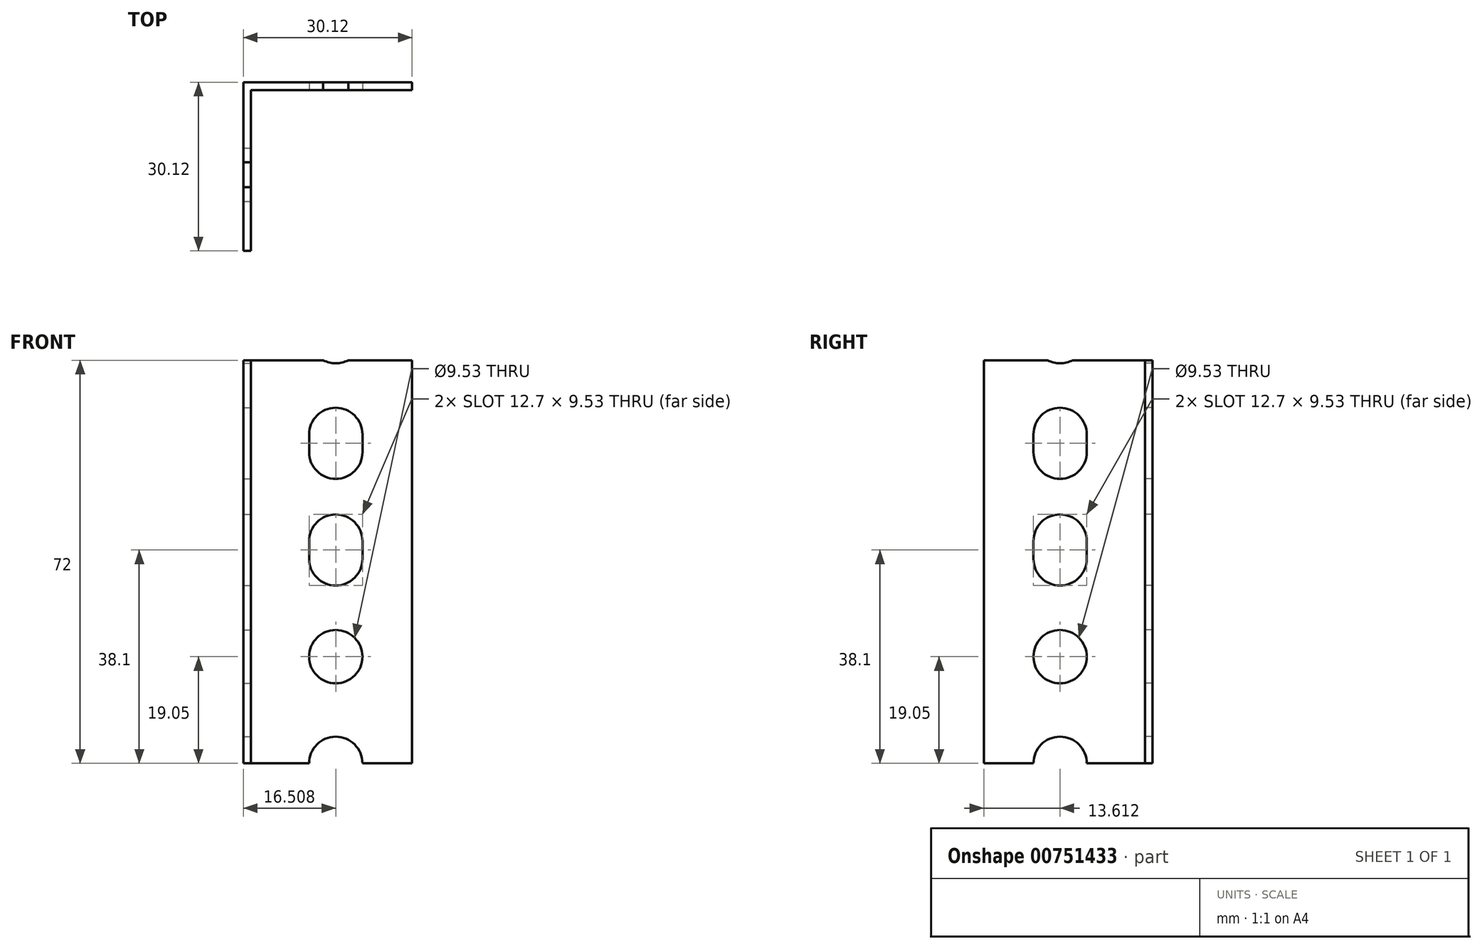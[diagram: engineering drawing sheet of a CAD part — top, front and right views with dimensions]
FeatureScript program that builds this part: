
annotation { "Feature Type Name" : "Feature", "Feature Type Description" : "" }
export const myFeature = defineFeature(function(context is Context, id is Id, definition is map)
    precondition{}
    {
        {
            assignVariable(context, id + "F0", {"name" : "height", "anyValue" : 72});
        }
        {
            var Q0;
            Q0=qCreatedBy(makeId("Top.planeOp"),FACE);
            var sketch = newSketch(context, id + "F1", { "sketchPlane" : qUnion([Q0])});
            skLineSegment(sketch, "E0", {"start": v(-1.37, -28.75) * mm, "end": v(-1.37, 1.37) * mm});
            skLineSegment(sketch, "E1", {"start": v(-1.37, 1.37) * mm, "end": v(28.75, 1.37) * mm});
            skLineSegment(sketch, "E2", {"start": v(28.75, 1.37) * mm, "end": v(28.75, 0) * mm});
            skLineSegment(sketch, "E3", {"start": v(28.75, 0) * mm, "end": v(0, 0) * mm});
            skLineSegment(sketch, "E4", {"start": v(0, 0) * mm, "end": v(0, -28.75) * mm});
            skLineSegment(sketch, "E5", {"start": v(0, -28.75) * mm, "end": v(-1.37, -28.75) * mm});
            skSolve(sketch);
        }
        {
            var Q0;
            Q0=makeQuery(id+"F1.imprint","IMPRINT",FACE,{"disambiguationData":[TD([[makeQuery(id+"F1.imprint","IMPRINT",EDGE,{"derivedFrom":sQuery(id+"F1.wireOp",EDGE,"E0")}),-1.0]])]});
            extrude(context, id + "F2", {"entities" : qUnion([Q0]), "depth" : (getVariable(context, 'height')) * mm, "offsetDistance" : 25.4 * mm});
        }
        {
            var Q0;
            Q0=makeQuery(id+"F2.opExtrude","SWEPT_FACE",FACE,{"disambiguationData":[OSD([sQuery(id+"F1.wireOp",EDGE,"E3")])]});
            var sketch = newSketch(context, id + "F3", { "sketchPlane" : qUnion([Q0])});
            skPoint(sketch, "E6", {"position": v(15.14, 19.05) * mm});
            skLineSegment(sketch, "E7", {"start": v(15.14, 0) * mm, "end": v(15.14, 1828.8) * mm, "construction": true});
            skCircle(sketch, "E8", {"center": v(15.14, 19.05) * mm, "radius": 4.76 * mm});
            skCircle(sketch, "E9", {"center": v(15.14, 0) * mm, "radius": 4.76 * mm});
            skPoint(sketch, "E10", {"position": v(15.14, 38.1) * mm});
            skPoint(sketch, "E11", {"position": v(15.14, 57.15) * mm});
            skArc(sketch, "E12", {"start": v(19.9, 39.69) * mm, "mid": v(15.14, 44.45) * mm, "end": v(10.38, 39.69) * mm});
            skArc(sketch, "E13", {"start": v(10.38, 36.51) * mm, "mid": v(15.14, 31.75) * mm, "end": v(19.9, 36.51) * mm});
            skLineSegment(sketch, "E14", {"start": v(19.9, 39.69) * mm, "end": v(19.9, 36.51) * mm});
            skLineSegment(sketch, "E15", {"start": v(10.38, 39.69) * mm, "end": v(10.38, 36.51) * mm});
            skArc(sketch, "E16", {"start": v(19.9, 58.74) * mm, "mid": v(15.14, 63.5) * mm, "end": v(10.38, 58.74) * mm});
            skArc(sketch, "E17", {"start": v(10.38, 55.56) * mm, "mid": v(15.14, 50.8) * mm, "end": v(19.9, 55.56) * mm});
            skLineSegment(sketch, "E18", {"start": v(19.9, 58.74) * mm, "end": v(19.9, 55.56) * mm});
            skLineSegment(sketch, "E19", {"start": v(10.38, 58.74) * mm, "end": v(10.38, 55.56) * mm});
            skPoint(sketch, "E20.0.1.0", {"position": v(15.14, 133.35) * mm});
            skArc(sketch, "E20.0.1.1", {"start": v(19.9, 134.94) * mm, "mid": v(15.14, 139.7) * mm, "end": v(10.38, 134.94) * mm});
            skPoint(sketch, "E20.0.1.2", {"position": v(15.14, 114.3) * mm});
            skPoint(sketch, "E20.0.1.3", {"position": v(15.14, 95.25) * mm});
            skArc(sketch, "E20.0.1.4", {"start": v(10.38, 131.76) * mm, "mid": v(15.14, 127) * mm, "end": v(19.9, 131.76) * mm});
            skCircle(sketch, "E20.0.1.5", {"center": v(15.14, 95.25) * mm, "radius": 4.76 * mm});
            skCircle(sketch, "E20.0.1.6", {"center": v(15.14, 76.2) * mm, "radius": 4.76 * mm});
            skArc(sketch, "E20.0.1.7", {"start": v(19.9, 115.89) * mm, "mid": v(15.14, 120.65) * mm, "end": v(10.38, 115.89) * mm});
            skArc(sketch, "E20.0.1.8", {"start": v(10.38, 112.71) * mm, "mid": v(15.14, 107.95) * mm, "end": v(19.9, 112.71) * mm});
            skPoint(sketch, "E20.0.1.9", {"position": v(15.14, 133.35) * mm});
            skPoint(sketch, "E20.0.1.10", {"position": v(15.14, 114.3) * mm});
            skLineSegment(sketch, "E20.0.1.11", {"start": v(10.38, 134.94) * mm, "end": v(10.38, 131.76) * mm});
            skLineSegment(sketch, "E20.0.1.12", {"start": v(19.9, 134.94) * mm, "end": v(19.9, 131.76) * mm});
            skLineSegment(sketch, "E20.0.1.13", {"start": v(19.9, 115.89) * mm, "end": v(19.9, 112.71) * mm});
            skLineSegment(sketch, "E20.0.1.14", {"start": v(10.38, 115.89) * mm, "end": v(10.38, 112.71) * mm});
            skPoint(sketch, "E20.0.2.0", {"position": v(15.14, 209.55) * mm});
            skArc(sketch, "E20.0.2.1", {"start": v(19.9, 211.14) * mm, "mid": v(15.14, 215.9) * mm, "end": v(10.38, 211.14) * mm});
            skPoint(sketch, "E20.0.2.2", {"position": v(15.14, 190.5) * mm});
            skPoint(sketch, "E20.0.2.3", {"position": v(15.14, 171.45) * mm});
            skArc(sketch, "E20.0.2.4", {"start": v(10.38, 207.96) * mm, "mid": v(15.14, 203.2) * mm, "end": v(19.9, 207.96) * mm});
            skCircle(sketch, "E20.0.2.5", {"center": v(15.14, 171.45) * mm, "radius": 4.76 * mm});
            skCircle(sketch, "E20.0.2.6", {"center": v(15.14, 152.4) * mm, "radius": 4.76 * mm});
            skArc(sketch, "E20.0.2.7", {"start": v(19.9, 192.09) * mm, "mid": v(15.14, 196.85) * mm, "end": v(10.38, 192.09) * mm});
            skArc(sketch, "E20.0.2.8", {"start": v(10.38, 188.91) * mm, "mid": v(15.14, 184.15) * mm, "end": v(19.9, 188.91) * mm});
            skPoint(sketch, "E20.0.2.9", {"position": v(15.14, 209.55) * mm});
            skPoint(sketch, "E20.0.2.10", {"position": v(15.14, 190.5) * mm});
            skLineSegment(sketch, "E20.0.2.11", {"start": v(10.38, 211.14) * mm, "end": v(10.38, 207.96) * mm});
            skLineSegment(sketch, "E20.0.2.12", {"start": v(19.9, 211.14) * mm, "end": v(19.9, 207.96) * mm});
            skLineSegment(sketch, "E20.0.2.13", {"start": v(19.9, 192.09) * mm, "end": v(19.9, 188.91) * mm});
            skLineSegment(sketch, "E20.0.2.14", {"start": v(10.38, 192.09) * mm, "end": v(10.38, 188.91) * mm});
            skPoint(sketch, "E20.0.3.0", {"position": v(15.14, 285.75) * mm});
            skArc(sketch, "E20.0.3.1", {"start": v(19.9, 287.34) * mm, "mid": v(15.14, 292.1) * mm, "end": v(10.38, 287.34) * mm});
            skPoint(sketch, "E20.0.3.2", {"position": v(15.14, 266.7) * mm});
            skPoint(sketch, "E20.0.3.3", {"position": v(15.14, 247.65) * mm});
            skArc(sketch, "E20.0.3.4", {"start": v(10.38, 284.16) * mm, "mid": v(15.14, 279.4) * mm, "end": v(19.9, 284.16) * mm});
            skCircle(sketch, "E20.0.3.5", {"center": v(15.14, 247.65) * mm, "radius": 4.76 * mm});
            skCircle(sketch, "E20.0.3.6", {"center": v(15.14, 228.6) * mm, "radius": 4.76 * mm});
            skArc(sketch, "E20.0.3.7", {"start": v(19.9, 268.29) * mm, "mid": v(15.14, 273.05) * mm, "end": v(10.38, 268.29) * mm});
            skArc(sketch, "E20.0.3.8", {"start": v(10.38, 265.11) * mm, "mid": v(15.14, 260.35) * mm, "end": v(19.9, 265.11) * mm});
            skPoint(sketch, "E20.0.3.9", {"position": v(15.14, 285.75) * mm});
            skPoint(sketch, "E20.0.3.10", {"position": v(15.14, 266.7) * mm});
            skLineSegment(sketch, "E20.0.3.11", {"start": v(10.38, 287.34) * mm, "end": v(10.38, 284.16) * mm});
            skLineSegment(sketch, "E20.0.3.12", {"start": v(19.9, 287.34) * mm, "end": v(19.9, 284.16) * mm});
            skLineSegment(sketch, "E20.0.3.13", {"start": v(19.9, 268.29) * mm, "end": v(19.9, 265.11) * mm});
            skLineSegment(sketch, "E20.0.3.14", {"start": v(10.38, 268.29) * mm, "end": v(10.38, 265.11) * mm});
            skPoint(sketch, "E20.0.4.0", {"position": v(15.14, 361.95) * mm});
            skArc(sketch, "E20.0.4.1", {"start": v(19.9, 363.54) * mm, "mid": v(15.14, 368.3) * mm, "end": v(10.38, 363.54) * mm});
            skPoint(sketch, "E20.0.4.2", {"position": v(15.14, 342.9) * mm});
            skPoint(sketch, "E20.0.4.3", {"position": v(15.14, 323.85) * mm});
            skArc(sketch, "E20.0.4.4", {"start": v(10.38, 360.36) * mm, "mid": v(15.14, 355.6) * mm, "end": v(19.9, 360.36) * mm});
            skCircle(sketch, "E20.0.4.5", {"center": v(15.14, 323.85) * mm, "radius": 4.76 * mm});
            skCircle(sketch, "E20.0.4.6", {"center": v(15.14, 304.8) * mm, "radius": 4.76 * mm});
            skArc(sketch, "E20.0.4.7", {"start": v(19.9, 344.49) * mm, "mid": v(15.14, 349.25) * mm, "end": v(10.38, 344.49) * mm});
            skArc(sketch, "E20.0.4.8", {"start": v(10.38, 341.31) * mm, "mid": v(15.14, 336.55) * mm, "end": v(19.9, 341.31) * mm});
            skPoint(sketch, "E20.0.4.9", {"position": v(15.14, 361.95) * mm});
            skPoint(sketch, "E20.0.4.10", {"position": v(15.14, 342.9) * mm});
            skLineSegment(sketch, "E20.0.4.11", {"start": v(10.38, 363.54) * mm, "end": v(10.38, 360.36) * mm});
            skLineSegment(sketch, "E20.0.4.12", {"start": v(19.9, 363.54) * mm, "end": v(19.9, 360.36) * mm});
            skLineSegment(sketch, "E20.0.4.13", {"start": v(19.9, 344.49) * mm, "end": v(19.9, 341.31) * mm});
            skLineSegment(sketch, "E20.0.4.14", {"start": v(10.38, 344.49) * mm, "end": v(10.38, 341.31) * mm});
            skPoint(sketch, "E20.0.5.0", {"position": v(15.14, 438.15) * mm});
            skArc(sketch, "E20.0.5.1", {"start": v(19.9, 439.74) * mm, "mid": v(15.14, 444.5) * mm, "end": v(10.38, 439.74) * mm});
            skPoint(sketch, "E20.0.5.2", {"position": v(15.14, 419.1) * mm});
            skPoint(sketch, "E20.0.5.3", {"position": v(15.14, 400.05) * mm});
            skArc(sketch, "E20.0.5.4", {"start": v(10.38, 436.56) * mm, "mid": v(15.14, 431.8) * mm, "end": v(19.9, 436.56) * mm});
            skCircle(sketch, "E20.0.5.5", {"center": v(15.14, 400.05) * mm, "radius": 4.76 * mm});
            skCircle(sketch, "E20.0.5.6", {"center": v(15.14, 381) * mm, "radius": 4.76 * mm});
            skArc(sketch, "E20.0.5.7", {"start": v(19.9, 420.69) * mm, "mid": v(15.14, 425.45) * mm, "end": v(10.38, 420.69) * mm});
            skArc(sketch, "E20.0.5.8", {"start": v(10.38, 417.51) * mm, "mid": v(15.14, 412.75) * mm, "end": v(19.9, 417.51) * mm});
            skPoint(sketch, "E20.0.5.9", {"position": v(15.14, 438.15) * mm});
            skPoint(sketch, "E20.0.5.10", {"position": v(15.14, 419.1) * mm});
            skLineSegment(sketch, "E20.0.5.11", {"start": v(10.38, 439.74) * mm, "end": v(10.38, 436.56) * mm});
            skLineSegment(sketch, "E20.0.5.12", {"start": v(19.9, 439.74) * mm, "end": v(19.9, 436.56) * mm});
            skLineSegment(sketch, "E20.0.5.13", {"start": v(19.9, 420.69) * mm, "end": v(19.9, 417.51) * mm});
            skLineSegment(sketch, "E20.0.5.14", {"start": v(10.38, 420.69) * mm, "end": v(10.38, 417.51) * mm});
            skPoint(sketch, "E20.0.6.0", {"position": v(15.14, 514.35) * mm});
            skArc(sketch, "E20.0.6.1", {"start": v(19.9, 515.94) * mm, "mid": v(15.14, 520.7) * mm, "end": v(10.38, 515.94) * mm});
            skPoint(sketch, "E20.0.6.2", {"position": v(15.14, 495.3) * mm});
            skPoint(sketch, "E20.0.6.3", {"position": v(15.14, 476.25) * mm});
            skArc(sketch, "E20.0.6.4", {"start": v(10.38, 512.76) * mm, "mid": v(15.14, 508) * mm, "end": v(19.9, 512.76) * mm});
            skCircle(sketch, "E20.0.6.5", {"center": v(15.14, 476.25) * mm, "radius": 4.76 * mm});
            skCircle(sketch, "E20.0.6.6", {"center": v(15.14, 457.2) * mm, "radius": 4.76 * mm});
            skArc(sketch, "E20.0.6.7", {"start": v(19.9, 496.89) * mm, "mid": v(15.14, 501.65) * mm, "end": v(10.38, 496.89) * mm});
            skArc(sketch, "E20.0.6.8", {"start": v(10.38, 493.71) * mm, "mid": v(15.14, 488.95) * mm, "end": v(19.9, 493.71) * mm});
            skPoint(sketch, "E20.0.6.9", {"position": v(15.14, 514.35) * mm});
            skPoint(sketch, "E20.0.6.10", {"position": v(15.14, 495.3) * mm});
            skLineSegment(sketch, "E20.0.6.11", {"start": v(10.38, 515.94) * mm, "end": v(10.38, 512.76) * mm});
            skLineSegment(sketch, "E20.0.6.12", {"start": v(19.9, 515.94) * mm, "end": v(19.9, 512.76) * mm});
            skLineSegment(sketch, "E20.0.6.13", {"start": v(19.9, 496.89) * mm, "end": v(19.9, 493.71) * mm});
            skLineSegment(sketch, "E20.0.6.14", {"start": v(10.38, 496.89) * mm, "end": v(10.38, 493.71) * mm});
            skPoint(sketch, "E20.0.7.0", {"position": v(15.14, 590.55) * mm});
            skArc(sketch, "E20.0.7.1", {"start": v(19.9, 592.14) * mm, "mid": v(15.14, 596.9) * mm, "end": v(10.38, 592.14) * mm});
            skPoint(sketch, "E20.0.7.2", {"position": v(15.14, 571.5) * mm});
            skPoint(sketch, "E20.0.7.3", {"position": v(15.14, 552.45) * mm});
            skArc(sketch, "E20.0.7.4", {"start": v(10.38, 588.96) * mm, "mid": v(15.14, 584.2) * mm, "end": v(19.9, 588.96) * mm});
            skCircle(sketch, "E20.0.7.5", {"center": v(15.14, 552.45) * mm, "radius": 4.76 * mm});
            skCircle(sketch, "E20.0.7.6", {"center": v(15.14, 533.4) * mm, "radius": 4.76 * mm});
            skArc(sketch, "E20.0.7.7", {"start": v(19.9, 573.09) * mm, "mid": v(15.14, 577.85) * mm, "end": v(10.38, 573.09) * mm});
            skArc(sketch, "E20.0.7.8", {"start": v(10.38, 569.91) * mm, "mid": v(15.14, 565.15) * mm, "end": v(19.9, 569.91) * mm});
            skPoint(sketch, "E20.0.7.9", {"position": v(15.14, 590.55) * mm});
            skPoint(sketch, "E20.0.7.10", {"position": v(15.14, 571.5) * mm});
            skLineSegment(sketch, "E20.0.7.11", {"start": v(10.38, 592.14) * mm, "end": v(10.38, 588.96) * mm});
            skLineSegment(sketch, "E20.0.7.12", {"start": v(19.9, 592.14) * mm, "end": v(19.9, 588.96) * mm});
            skLineSegment(sketch, "E20.0.7.13", {"start": v(19.9, 573.09) * mm, "end": v(19.9, 569.91) * mm});
            skLineSegment(sketch, "E20.0.7.14", {"start": v(10.38, 573.09) * mm, "end": v(10.38, 569.91) * mm});
            skPoint(sketch, "E20.0.8.0", {"position": v(15.14, 666.75) * mm});
            skArc(sketch, "E20.0.8.1", {"start": v(19.9, 668.34) * mm, "mid": v(15.14, 673.1) * mm, "end": v(10.38, 668.34) * mm});
            skPoint(sketch, "E20.0.8.2", {"position": v(15.14, 647.7) * mm});
            skPoint(sketch, "E20.0.8.3", {"position": v(15.14, 628.65) * mm});
            skArc(sketch, "E20.0.8.4", {"start": v(10.38, 665.16) * mm, "mid": v(15.14, 660.4) * mm, "end": v(19.9, 665.16) * mm});
            skCircle(sketch, "E20.0.8.5", {"center": v(15.14, 628.65) * mm, "radius": 4.76 * mm});
            skCircle(sketch, "E20.0.8.6", {"center": v(15.14, 609.6) * mm, "radius": 4.76 * mm});
            skArc(sketch, "E20.0.8.7", {"start": v(19.9, 649.29) * mm, "mid": v(15.14, 654.05) * mm, "end": v(10.38, 649.29) * mm});
            skArc(sketch, "E20.0.8.8", {"start": v(10.38, 646.11) * mm, "mid": v(15.14, 641.35) * mm, "end": v(19.9, 646.11) * mm});
            skPoint(sketch, "E20.0.8.9", {"position": v(15.14, 666.75) * mm});
            skPoint(sketch, "E20.0.8.10", {"position": v(15.14, 647.7) * mm});
            skLineSegment(sketch, "E20.0.8.11", {"start": v(10.38, 668.34) * mm, "end": v(10.38, 665.16) * mm});
            skLineSegment(sketch, "E20.0.8.12", {"start": v(19.9, 668.34) * mm, "end": v(19.9, 665.16) * mm});
            skLineSegment(sketch, "E20.0.8.13", {"start": v(19.9, 649.29) * mm, "end": v(19.9, 646.11) * mm});
            skLineSegment(sketch, "E20.0.8.14", {"start": v(10.38, 649.29) * mm, "end": v(10.38, 646.11) * mm});
            skPoint(sketch, "E20.0.9.0", {"position": v(15.14, 742.95) * mm});
            skArc(sketch, "E20.0.9.1", {"start": v(19.9, 744.54) * mm, "mid": v(15.14, 749.3) * mm, "end": v(10.38, 744.54) * mm});
            skPoint(sketch, "E20.0.9.2", {"position": v(15.14, 723.9) * mm});
            skPoint(sketch, "E20.0.9.3", {"position": v(15.14, 704.85) * mm});
            skArc(sketch, "E20.0.9.4", {"start": v(10.38, 741.36) * mm, "mid": v(15.14, 736.6) * mm, "end": v(19.9, 741.36) * mm});
            skCircle(sketch, "E20.0.9.5", {"center": v(15.14, 704.85) * mm, "radius": 4.76 * mm});
            skCircle(sketch, "E20.0.9.6", {"center": v(15.14, 685.8) * mm, "radius": 4.76 * mm});
            skArc(sketch, "E20.0.9.7", {"start": v(19.9, 725.49) * mm, "mid": v(15.14, 730.25) * mm, "end": v(10.38, 725.49) * mm});
            skArc(sketch, "E20.0.9.8", {"start": v(10.38, 722.31) * mm, "mid": v(15.14, 717.55) * mm, "end": v(19.9, 722.31) * mm});
            skPoint(sketch, "E20.0.9.9", {"position": v(15.14, 742.95) * mm});
            skPoint(sketch, "E20.0.9.10", {"position": v(15.14, 723.9) * mm});
            skLineSegment(sketch, "E20.0.9.11", {"start": v(10.38, 744.54) * mm, "end": v(10.38, 741.36) * mm});
            skLineSegment(sketch, "E20.0.9.12", {"start": v(19.9, 744.54) * mm, "end": v(19.9, 741.36) * mm});
            skLineSegment(sketch, "E20.0.9.13", {"start": v(19.9, 725.49) * mm, "end": v(19.9, 722.31) * mm});
            skLineSegment(sketch, "E20.0.9.14", {"start": v(10.38, 725.49) * mm, "end": v(10.38, 722.31) * mm});
            skPoint(sketch, "E20.0.10.0", {"position": v(15.14, 819.15) * mm});
            skArc(sketch, "E20.0.10.1", {"start": v(19.9, 820.74) * mm, "mid": v(15.14, 825.5) * mm, "end": v(10.38, 820.74) * mm});
            skPoint(sketch, "E20.0.10.2", {"position": v(15.14, 800.1) * mm});
            skPoint(sketch, "E20.0.10.3", {"position": v(15.14, 781.05) * mm});
            skArc(sketch, "E20.0.10.4", {"start": v(10.38, 817.56) * mm, "mid": v(15.14, 812.8) * mm, "end": v(19.9, 817.56) * mm});
            skCircle(sketch, "E20.0.10.5", {"center": v(15.14, 781.05) * mm, "radius": 4.76 * mm});
            skCircle(sketch, "E20.0.10.6", {"center": v(15.14, 762) * mm, "radius": 4.76 * mm});
            skArc(sketch, "E20.0.10.7", {"start": v(19.9, 801.69) * mm, "mid": v(15.14, 806.45) * mm, "end": v(10.38, 801.69) * mm});
            skArc(sketch, "E20.0.10.8", {"start": v(10.38, 798.51) * mm, "mid": v(15.14, 793.75) * mm, "end": v(19.9, 798.51) * mm});
            skPoint(sketch, "E20.0.10.9", {"position": v(15.14, 819.15) * mm});
            skPoint(sketch, "E20.0.10.10", {"position": v(15.14, 800.1) * mm});
            skLineSegment(sketch, "E20.0.10.11", {"start": v(10.38, 820.74) * mm, "end": v(10.38, 817.56) * mm});
            skLineSegment(sketch, "E20.0.10.12", {"start": v(19.9, 820.74) * mm, "end": v(19.9, 817.56) * mm});
            skLineSegment(sketch, "E20.0.10.13", {"start": v(19.9, 801.69) * mm, "end": v(19.9, 798.51) * mm});
            skLineSegment(sketch, "E20.0.10.14", {"start": v(10.38, 801.69) * mm, "end": v(10.38, 798.51) * mm});
            skPoint(sketch, "E20.0.11.0", {"position": v(15.14, 895.35) * mm});
            skArc(sketch, "E20.0.11.1", {"start": v(19.9, 896.94) * mm, "mid": v(15.14, 901.7) * mm, "end": v(10.38, 896.94) * mm});
            skPoint(sketch, "E20.0.11.2", {"position": v(15.14, 876.3) * mm});
            skPoint(sketch, "E20.0.11.3", {"position": v(15.14, 857.25) * mm});
            skArc(sketch, "E20.0.11.4", {"start": v(10.38, 893.76) * mm, "mid": v(15.14, 889) * mm, "end": v(19.9, 893.76) * mm});
            skCircle(sketch, "E20.0.11.5", {"center": v(15.14, 857.25) * mm, "radius": 4.76 * mm});
            skCircle(sketch, "E20.0.11.6", {"center": v(15.14, 838.2) * mm, "radius": 4.76 * mm});
            skArc(sketch, "E20.0.11.7", {"start": v(19.9, 877.89) * mm, "mid": v(15.14, 882.65) * mm, "end": v(10.38, 877.89) * mm});
            skArc(sketch, "E20.0.11.8", {"start": v(10.38, 874.71) * mm, "mid": v(15.14, 869.95) * mm, "end": v(19.9, 874.71) * mm});
            skPoint(sketch, "E20.0.11.9", {"position": v(15.14, 895.35) * mm});
            skPoint(sketch, "E20.0.11.10", {"position": v(15.14, 876.3) * mm});
            skLineSegment(sketch, "E20.0.11.11", {"start": v(10.38, 896.94) * mm, "end": v(10.38, 893.76) * mm});
            skLineSegment(sketch, "E20.0.11.12", {"start": v(19.9, 896.94) * mm, "end": v(19.9, 893.76) * mm});
            skLineSegment(sketch, "E20.0.11.13", {"start": v(19.9, 877.89) * mm, "end": v(19.9, 874.71) * mm});
            skLineSegment(sketch, "E20.0.11.14", {"start": v(10.38, 877.89) * mm, "end": v(10.38, 874.71) * mm});
            skPoint(sketch, "E20.0.12.0", {"position": v(15.14, 971.55) * mm});
            skArc(sketch, "E20.0.12.1", {"start": v(19.9, 973.14) * mm, "mid": v(15.14, 977.9) * mm, "end": v(10.38, 973.14) * mm});
            skPoint(sketch, "E20.0.12.2", {"position": v(15.14, 952.5) * mm});
            skPoint(sketch, "E20.0.12.3", {"position": v(15.14, 933.45) * mm});
            skArc(sketch, "E20.0.12.4", {"start": v(10.38, 969.96) * mm, "mid": v(15.14, 965.2) * mm, "end": v(19.9, 969.96) * mm});
            skCircle(sketch, "E20.0.12.5", {"center": v(15.14, 933.45) * mm, "radius": 4.76 * mm});
            skCircle(sketch, "E20.0.12.6", {"center": v(15.14, 914.4) * mm, "radius": 4.76 * mm});
            skArc(sketch, "E20.0.12.7", {"start": v(19.9, 954.09) * mm, "mid": v(15.14, 958.85) * mm, "end": v(10.38, 954.09) * mm});
            skArc(sketch, "E20.0.12.8", {"start": v(10.38, 950.91) * mm, "mid": v(15.14, 946.15) * mm, "end": v(19.9, 950.91) * mm});
            skPoint(sketch, "E20.0.12.9", {"position": v(15.14, 971.55) * mm});
            skPoint(sketch, "E20.0.12.10", {"position": v(15.14, 952.5) * mm});
            skLineSegment(sketch, "E20.0.12.11", {"start": v(10.38, 973.14) * mm, "end": v(10.38, 969.96) * mm});
            skLineSegment(sketch, "E20.0.12.12", {"start": v(19.9, 973.14) * mm, "end": v(19.9, 969.96) * mm});
            skLineSegment(sketch, "E20.0.12.13", {"start": v(19.9, 954.09) * mm, "end": v(19.9, 950.91) * mm});
            skLineSegment(sketch, "E20.0.12.14", {"start": v(10.38, 954.09) * mm, "end": v(10.38, 950.91) * mm});
            skPoint(sketch, "E20.0.13.0", {"position": v(15.14, 1047.75) * mm});
            skArc(sketch, "E20.0.13.1", {"start": v(19.9, 1049.34) * mm, "mid": v(15.14, 1054.1) * mm, "end": v(10.38, 1049.34) * mm});
            skPoint(sketch, "E20.0.13.2", {"position": v(15.14, 1028.7) * mm});
            skPoint(sketch, "E20.0.13.3", {"position": v(15.14, 1009.65) * mm});
            skArc(sketch, "E20.0.13.4", {"start": v(10.38, 1046.16) * mm, "mid": v(15.14, 1041.4) * mm, "end": v(19.9, 1046.16) * mm});
            skCircle(sketch, "E20.0.13.5", {"center": v(15.14, 1009.65) * mm, "radius": 4.76 * mm});
            skCircle(sketch, "E20.0.13.6", {"center": v(15.14, 990.6) * mm, "radius": 4.76 * mm});
            skArc(sketch, "E20.0.13.7", {"start": v(19.9, 1030.29) * mm, "mid": v(15.14, 1035.05) * mm, "end": v(10.38, 1030.29) * mm});
            skArc(sketch, "E20.0.13.8", {"start": v(10.38, 1027.11) * mm, "mid": v(15.14, 1022.35) * mm, "end": v(19.9, 1027.11) * mm});
            skPoint(sketch, "E20.0.13.9", {"position": v(15.14, 1047.75) * mm});
            skPoint(sketch, "E20.0.13.10", {"position": v(15.14, 1028.7) * mm});
            skLineSegment(sketch, "E20.0.13.11", {"start": v(10.38, 1049.34) * mm, "end": v(10.38, 1046.16) * mm});
            skLineSegment(sketch, "E20.0.13.12", {"start": v(19.9, 1049.34) * mm, "end": v(19.9, 1046.16) * mm});
            skLineSegment(sketch, "E20.0.13.13", {"start": v(19.9, 1030.29) * mm, "end": v(19.9, 1027.11) * mm});
            skLineSegment(sketch, "E20.0.13.14", {"start": v(10.38, 1030.29) * mm, "end": v(10.38, 1027.11) * mm});
            skPoint(sketch, "E20.0.14.0", {"position": v(15.14, 1123.95) * mm});
            skArc(sketch, "E20.0.14.1", {"start": v(19.9, 1125.54) * mm, "mid": v(15.14, 1130.3) * mm, "end": v(10.38, 1125.54) * mm});
            skPoint(sketch, "E20.0.14.2", {"position": v(15.14, 1104.9) * mm});
            skPoint(sketch, "E20.0.14.3", {"position": v(15.14, 1085.85) * mm});
            skArc(sketch, "E20.0.14.4", {"start": v(10.38, 1122.36) * mm, "mid": v(15.14, 1117.6) * mm, "end": v(19.9, 1122.36) * mm});
            skCircle(sketch, "E20.0.14.5", {"center": v(15.14, 1085.85) * mm, "radius": 4.76 * mm});
            skCircle(sketch, "E20.0.14.6", {"center": v(15.14, 1066.8) * mm, "radius": 4.76 * mm});
            skArc(sketch, "E20.0.14.7", {"start": v(19.9, 1106.49) * mm, "mid": v(15.14, 1111.25) * mm, "end": v(10.38, 1106.49) * mm});
            skArc(sketch, "E20.0.14.8", {"start": v(10.38, 1103.31) * mm, "mid": v(15.14, 1098.55) * mm, "end": v(19.9, 1103.31) * mm});
            skPoint(sketch, "E20.0.14.9", {"position": v(15.14, 1123.95) * mm});
            skPoint(sketch, "E20.0.14.10", {"position": v(15.14, 1104.9) * mm});
            skLineSegment(sketch, "E20.0.14.11", {"start": v(10.38, 1125.54) * mm, "end": v(10.38, 1122.36) * mm});
            skLineSegment(sketch, "E20.0.14.12", {"start": v(19.9, 1125.54) * mm, "end": v(19.9, 1122.36) * mm});
            skLineSegment(sketch, "E20.0.14.13", {"start": v(19.9, 1106.49) * mm, "end": v(19.9, 1103.31) * mm});
            skLineSegment(sketch, "E20.0.14.14", {"start": v(10.38, 1106.49) * mm, "end": v(10.38, 1103.31) * mm});
            skPoint(sketch, "E20.0.15.0", {"position": v(15.14, 1200.15) * mm});
            skArc(sketch, "E20.0.15.1", {"start": v(19.9, 1201.74) * mm, "mid": v(15.14, 1206.5) * mm, "end": v(10.38, 1201.74) * mm});
            skPoint(sketch, "E20.0.15.2", {"position": v(15.14, 1181.1) * mm});
            skPoint(sketch, "E20.0.15.3", {"position": v(15.14, 1162.05) * mm});
            skArc(sketch, "E20.0.15.4", {"start": v(10.38, 1198.56) * mm, "mid": v(15.14, 1193.8) * mm, "end": v(19.9, 1198.56) * mm});
            skCircle(sketch, "E20.0.15.5", {"center": v(15.14, 1162.05) * mm, "radius": 4.76 * mm});
            skCircle(sketch, "E20.0.15.6", {"center": v(15.14, 1143) * mm, "radius": 4.76 * mm});
            skArc(sketch, "E20.0.15.7", {"start": v(19.9, 1182.69) * mm, "mid": v(15.14, 1187.45) * mm, "end": v(10.38, 1182.69) * mm});
            skArc(sketch, "E20.0.15.8", {"start": v(10.38, 1179.51) * mm, "mid": v(15.14, 1174.75) * mm, "end": v(19.9, 1179.51) * mm});
            skPoint(sketch, "E20.0.15.9", {"position": v(15.14, 1200.15) * mm});
            skPoint(sketch, "E20.0.15.10", {"position": v(15.14, 1181.1) * mm});
            skLineSegment(sketch, "E20.0.15.11", {"start": v(10.38, 1201.74) * mm, "end": v(10.38, 1198.56) * mm});
            skLineSegment(sketch, "E20.0.15.12", {"start": v(19.9, 1201.74) * mm, "end": v(19.9, 1198.56) * mm});
            skLineSegment(sketch, "E20.0.15.13", {"start": v(19.9, 1182.69) * mm, "end": v(19.9, 1179.51) * mm});
            skLineSegment(sketch, "E20.0.15.14", {"start": v(10.38, 1182.69) * mm, "end": v(10.38, 1179.51) * mm});
            skPoint(sketch, "E20.0.16.0", {"position": v(15.14, 1276.35) * mm});
            skArc(sketch, "E20.0.16.1", {"start": v(19.9, 1277.94) * mm, "mid": v(15.14, 1282.7) * mm, "end": v(10.38, 1277.94) * mm});
            skPoint(sketch, "E20.0.16.2", {"position": v(15.14, 1257.3) * mm});
            skPoint(sketch, "E20.0.16.3", {"position": v(15.14, 1238.25) * mm});
            skArc(sketch, "E20.0.16.4", {"start": v(10.38, 1274.76) * mm, "mid": v(15.14, 1270) * mm, "end": v(19.9, 1274.76) * mm});
            skCircle(sketch, "E20.0.16.5", {"center": v(15.14, 1238.25) * mm, "radius": 4.76 * mm});
            skCircle(sketch, "E20.0.16.6", {"center": v(15.14, 1219.2) * mm, "radius": 4.76 * mm});
            skArc(sketch, "E20.0.16.7", {"start": v(19.9, 1258.89) * mm, "mid": v(15.14, 1263.65) * mm, "end": v(10.38, 1258.89) * mm});
            skArc(sketch, "E20.0.16.8", {"start": v(10.38, 1255.71) * mm, "mid": v(15.14, 1250.95) * mm, "end": v(19.9, 1255.71) * mm});
            skPoint(sketch, "E20.0.16.9", {"position": v(15.14, 1276.35) * mm});
            skPoint(sketch, "E20.0.16.10", {"position": v(15.14, 1257.3) * mm});
            skLineSegment(sketch, "E20.0.16.11", {"start": v(10.38, 1277.94) * mm, "end": v(10.38, 1274.76) * mm});
            skLineSegment(sketch, "E20.0.16.12", {"start": v(19.9, 1277.94) * mm, "end": v(19.9, 1274.76) * mm});
            skLineSegment(sketch, "E20.0.16.13", {"start": v(19.9, 1258.89) * mm, "end": v(19.9, 1255.71) * mm});
            skLineSegment(sketch, "E20.0.16.14", {"start": v(10.38, 1258.89) * mm, "end": v(10.38, 1255.71) * mm});
            skPoint(sketch, "E20.0.17.0", {"position": v(15.14, 1352.55) * mm});
            skArc(sketch, "E20.0.17.1", {"start": v(19.9, 1354.14) * mm, "mid": v(15.14, 1358.9) * mm, "end": v(10.38, 1354.14) * mm});
            skPoint(sketch, "E20.0.17.2", {"position": v(15.14, 1333.5) * mm});
            skPoint(sketch, "E20.0.17.3", {"position": v(15.14, 1314.45) * mm});
            skArc(sketch, "E20.0.17.4", {"start": v(10.38, 1350.96) * mm, "mid": v(15.14, 1346.2) * mm, "end": v(19.9, 1350.96) * mm});
            skCircle(sketch, "E20.0.17.5", {"center": v(15.14, 1314.45) * mm, "radius": 4.76 * mm});
            skCircle(sketch, "E20.0.17.6", {"center": v(15.14, 1295.4) * mm, "radius": 4.76 * mm});
            skArc(sketch, "E20.0.17.7", {"start": v(19.9, 1335.09) * mm, "mid": v(15.14, 1339.85) * mm, "end": v(10.38, 1335.09) * mm});
            skArc(sketch, "E20.0.17.8", {"start": v(10.38, 1331.91) * mm, "mid": v(15.14, 1327.15) * mm, "end": v(19.9, 1331.91) * mm});
            skPoint(sketch, "E20.0.17.9", {"position": v(15.14, 1352.55) * mm});
            skPoint(sketch, "E20.0.17.10", {"position": v(15.14, 1333.5) * mm});
            skLineSegment(sketch, "E20.0.17.11", {"start": v(10.38, 1354.14) * mm, "end": v(10.38, 1350.96) * mm});
            skLineSegment(sketch, "E20.0.17.12", {"start": v(19.9, 1354.14) * mm, "end": v(19.9, 1350.96) * mm});
            skLineSegment(sketch, "E20.0.17.13", {"start": v(19.9, 1335.09) * mm, "end": v(19.9, 1331.91) * mm});
            skLineSegment(sketch, "E20.0.17.14", {"start": v(10.38, 1335.09) * mm, "end": v(10.38, 1331.91) * mm});
            skPoint(sketch, "E20.0.18.0", {"position": v(15.14, 1428.75) * mm});
            skArc(sketch, "E20.0.18.1", {"start": v(19.9, 1430.34) * mm, "mid": v(15.14, 1435.1) * mm, "end": v(10.38, 1430.34) * mm});
            skPoint(sketch, "E20.0.18.2", {"position": v(15.14, 1409.7) * mm});
            skPoint(sketch, "E20.0.18.3", {"position": v(15.14, 1390.65) * mm});
            skArc(sketch, "E20.0.18.4", {"start": v(10.38, 1427.16) * mm, "mid": v(15.14, 1422.4) * mm, "end": v(19.9, 1427.16) * mm});
            skCircle(sketch, "E20.0.18.5", {"center": v(15.14, 1390.65) * mm, "radius": 4.76 * mm});
            skCircle(sketch, "E20.0.18.6", {"center": v(15.14, 1371.6) * mm, "radius": 4.76 * mm});
            skArc(sketch, "E20.0.18.7", {"start": v(19.9, 1411.29) * mm, "mid": v(15.14, 1416.05) * mm, "end": v(10.38, 1411.29) * mm});
            skArc(sketch, "E20.0.18.8", {"start": v(10.38, 1408.11) * mm, "mid": v(15.14, 1403.35) * mm, "end": v(19.9, 1408.11) * mm});
            skPoint(sketch, "E20.0.18.9", {"position": v(15.14, 1428.75) * mm});
            skPoint(sketch, "E20.0.18.10", {"position": v(15.14, 1409.7) * mm});
            skLineSegment(sketch, "E20.0.18.11", {"start": v(10.38, 1430.34) * mm, "end": v(10.38, 1427.16) * mm});
            skLineSegment(sketch, "E20.0.18.12", {"start": v(19.9, 1430.34) * mm, "end": v(19.9, 1427.16) * mm});
            skLineSegment(sketch, "E20.0.18.13", {"start": v(19.9, 1411.29) * mm, "end": v(19.9, 1408.11) * mm});
            skLineSegment(sketch, "E20.0.18.14", {"start": v(10.38, 1411.29) * mm, "end": v(10.38, 1408.11) * mm});
            skPoint(sketch, "E20.0.19.0", {"position": v(15.14, 1504.95) * mm});
            skArc(sketch, "E20.0.19.1", {"start": v(19.9, 1506.54) * mm, "mid": v(15.14, 1511.3) * mm, "end": v(10.38, 1506.54) * mm});
            skPoint(sketch, "E20.0.19.2", {"position": v(15.14, 1485.9) * mm});
            skPoint(sketch, "E20.0.19.3", {"position": v(15.14, 1466.85) * mm});
            skArc(sketch, "E20.0.19.4", {"start": v(10.38, 1503.36) * mm, "mid": v(15.14, 1498.6) * mm, "end": v(19.9, 1503.36) * mm});
            skCircle(sketch, "E20.0.19.5", {"center": v(15.14, 1466.85) * mm, "radius": 4.76 * mm});
            skCircle(sketch, "E20.0.19.6", {"center": v(15.14, 1447.8) * mm, "radius": 4.76 * mm});
            skArc(sketch, "E20.0.19.7", {"start": v(19.9, 1487.49) * mm, "mid": v(15.14, 1492.25) * mm, "end": v(10.38, 1487.49) * mm});
            skArc(sketch, "E20.0.19.8", {"start": v(10.38, 1484.31) * mm, "mid": v(15.14, 1479.55) * mm, "end": v(19.9, 1484.31) * mm});
            skPoint(sketch, "E20.0.19.9", {"position": v(15.14, 1504.95) * mm});
            skPoint(sketch, "E20.0.19.10", {"position": v(15.14, 1485.9) * mm});
            skLineSegment(sketch, "E20.0.19.11", {"start": v(10.38, 1506.54) * mm, "end": v(10.38, 1503.36) * mm});
            skLineSegment(sketch, "E20.0.19.12", {"start": v(19.9, 1506.54) * mm, "end": v(19.9, 1503.36) * mm});
            skLineSegment(sketch, "E20.0.19.13", {"start": v(19.9, 1487.49) * mm, "end": v(19.9, 1484.31) * mm});
            skLineSegment(sketch, "E20.0.19.14", {"start": v(10.38, 1487.49) * mm, "end": v(10.38, 1484.31) * mm});
            skPoint(sketch, "E20.0.20.0", {"position": v(15.14, 1581.15) * mm});
            skArc(sketch, "E20.0.20.1", {"start": v(19.9, 1582.74) * mm, "mid": v(15.14, 1587.5) * mm, "end": v(10.38, 1582.74) * mm});
            skPoint(sketch, "E20.0.20.2", {"position": v(15.14, 1562.1) * mm});
            skPoint(sketch, "E20.0.20.3", {"position": v(15.14, 1543.05) * mm});
            skArc(sketch, "E20.0.20.4", {"start": v(10.38, 1579.56) * mm, "mid": v(15.14, 1574.8) * mm, "end": v(19.9, 1579.56) * mm});
            skCircle(sketch, "E20.0.20.5", {"center": v(15.14, 1543.05) * mm, "radius": 4.76 * mm});
            skCircle(sketch, "E20.0.20.6", {"center": v(15.14, 1524) * mm, "radius": 4.76 * mm});
            skArc(sketch, "E20.0.20.7", {"start": v(19.9, 1563.69) * mm, "mid": v(15.14, 1568.45) * mm, "end": v(10.38, 1563.69) * mm});
            skArc(sketch, "E20.0.20.8", {"start": v(10.38, 1560.51) * mm, "mid": v(15.14, 1555.75) * mm, "end": v(19.9, 1560.51) * mm});
            skPoint(sketch, "E20.0.20.9", {"position": v(15.14, 1581.15) * mm});
            skPoint(sketch, "E20.0.20.10", {"position": v(15.14, 1562.1) * mm});
            skLineSegment(sketch, "E20.0.20.11", {"start": v(10.38, 1582.74) * mm, "end": v(10.38, 1579.56) * mm});
            skLineSegment(sketch, "E20.0.20.12", {"start": v(19.9, 1582.74) * mm, "end": v(19.9, 1579.56) * mm});
            skLineSegment(sketch, "E20.0.20.13", {"start": v(19.9, 1563.69) * mm, "end": v(19.9, 1560.51) * mm});
            skLineSegment(sketch, "E20.0.20.14", {"start": v(10.38, 1563.69) * mm, "end": v(10.38, 1560.51) * mm});
            skPoint(sketch, "E20.0.21.0", {"position": v(15.14, 1657.35) * mm});
            skArc(sketch, "E20.0.21.1", {"start": v(19.9, 1658.94) * mm, "mid": v(15.14, 1663.7) * mm, "end": v(10.38, 1658.94) * mm});
            skPoint(sketch, "E20.0.21.2", {"position": v(15.14, 1638.3) * mm});
            skPoint(sketch, "E20.0.21.3", {"position": v(15.14, 1619.25) * mm});
            skArc(sketch, "E20.0.21.4", {"start": v(10.38, 1655.76) * mm, "mid": v(15.14, 1651) * mm, "end": v(19.9, 1655.76) * mm});
            skCircle(sketch, "E20.0.21.5", {"center": v(15.14, 1619.25) * mm, "radius": 4.76 * mm});
            skCircle(sketch, "E20.0.21.6", {"center": v(15.14, 1600.2) * mm, "radius": 4.76 * mm});
            skArc(sketch, "E20.0.21.7", {"start": v(19.9, 1639.89) * mm, "mid": v(15.14, 1644.65) * mm, "end": v(10.38, 1639.89) * mm});
            skArc(sketch, "E20.0.21.8", {"start": v(10.38, 1636.71) * mm, "mid": v(15.14, 1631.95) * mm, "end": v(19.9, 1636.71) * mm});
            skPoint(sketch, "E20.0.21.9", {"position": v(15.14, 1657.35) * mm});
            skPoint(sketch, "E20.0.21.10", {"position": v(15.14, 1638.3) * mm});
            skLineSegment(sketch, "E20.0.21.11", {"start": v(10.38, 1658.94) * mm, "end": v(10.38, 1655.76) * mm});
            skLineSegment(sketch, "E20.0.21.12", {"start": v(19.9, 1658.94) * mm, "end": v(19.9, 1655.76) * mm});
            skLineSegment(sketch, "E20.0.21.13", {"start": v(19.9, 1639.89) * mm, "end": v(19.9, 1636.71) * mm});
            skLineSegment(sketch, "E20.0.21.14", {"start": v(10.38, 1639.89) * mm, "end": v(10.38, 1636.71) * mm});
            skPoint(sketch, "E20.0.22.0", {"position": v(15.14, 1733.55) * mm});
            skArc(sketch, "E20.0.22.1", {"start": v(19.9, 1735.14) * mm, "mid": v(15.14, 1739.9) * mm, "end": v(10.38, 1735.14) * mm});
            skPoint(sketch, "E20.0.22.2", {"position": v(15.14, 1714.5) * mm});
            skPoint(sketch, "E20.0.22.3", {"position": v(15.14, 1695.45) * mm});
            skArc(sketch, "E20.0.22.4", {"start": v(10.38, 1731.96) * mm, "mid": v(15.14, 1727.2) * mm, "end": v(19.9, 1731.96) * mm});
            skCircle(sketch, "E20.0.22.5", {"center": v(15.14, 1695.45) * mm, "radius": 4.76 * mm});
            skCircle(sketch, "E20.0.22.6", {"center": v(15.14, 1676.4) * mm, "radius": 4.76 * mm});
            skArc(sketch, "E20.0.22.7", {"start": v(19.9, 1716.09) * mm, "mid": v(15.14, 1720.85) * mm, "end": v(10.38, 1716.09) * mm});
            skArc(sketch, "E20.0.22.8", {"start": v(10.38, 1712.91) * mm, "mid": v(15.14, 1708.15) * mm, "end": v(19.9, 1712.91) * mm});
            skPoint(sketch, "E20.0.22.9", {"position": v(15.14, 1733.55) * mm});
            skPoint(sketch, "E20.0.22.10", {"position": v(15.14, 1714.5) * mm});
            skLineSegment(sketch, "E20.0.22.11", {"start": v(10.38, 1735.14) * mm, "end": v(10.38, 1731.96) * mm});
            skLineSegment(sketch, "E20.0.22.12", {"start": v(19.9, 1735.14) * mm, "end": v(19.9, 1731.96) * mm});
            skLineSegment(sketch, "E20.0.22.13", {"start": v(19.9, 1716.09) * mm, "end": v(19.9, 1712.91) * mm});
            skLineSegment(sketch, "E20.0.22.14", {"start": v(10.38, 1716.09) * mm, "end": v(10.38, 1712.91) * mm});
            skPoint(sketch, "E20.0.23.0", {"position": v(15.14, 1809.75) * mm});
            skArc(sketch, "E20.0.23.1", {"start": v(19.9, 1811.34) * mm, "mid": v(15.14, 1816.1) * mm, "end": v(10.38, 1811.34) * mm});
            skPoint(sketch, "E20.0.23.2", {"position": v(15.14, 1790.7) * mm});
            skPoint(sketch, "E20.0.23.3", {"position": v(15.14, 1771.65) * mm});
            skArc(sketch, "E20.0.23.4", {"start": v(10.38, 1808.16) * mm, "mid": v(15.14, 1803.4) * mm, "end": v(19.9, 1808.16) * mm});
            skCircle(sketch, "E20.0.23.5", {"center": v(15.14, 1771.65) * mm, "radius": 4.76 * mm});
            skCircle(sketch, "E20.0.23.6", {"center": v(15.14, 1752.6) * mm, "radius": 4.76 * mm});
            skArc(sketch, "E20.0.23.7", {"start": v(19.9, 1792.29) * mm, "mid": v(15.14, 1797.05) * mm, "end": v(10.38, 1792.29) * mm});
            skArc(sketch, "E20.0.23.8", {"start": v(10.38, 1789.11) * mm, "mid": v(15.14, 1784.35) * mm, "end": v(19.9, 1789.11) * mm});
            skPoint(sketch, "E20.0.23.9", {"position": v(15.14, 1809.75) * mm});
            skPoint(sketch, "E20.0.23.10", {"position": v(15.14, 1790.7) * mm});
            skLineSegment(sketch, "E20.0.23.11", {"start": v(10.38, 1811.34) * mm, "end": v(10.38, 1808.16) * mm});
            skLineSegment(sketch, "E20.0.23.12", {"start": v(19.9, 1811.34) * mm, "end": v(19.9, 1808.16) * mm});
            skLineSegment(sketch, "E20.0.23.13", {"start": v(19.9, 1792.29) * mm, "end": v(19.9, 1789.11) * mm});
            skLineSegment(sketch, "E20.0.23.14", {"start": v(10.38, 1792.29) * mm, "end": v(10.38, 1789.11) * mm});
            skLineSegment(sketch, "E20.direction1", {"start": v(15.14, 0) * mm, "end": v(40.54, 0) * mm, "construction": true});
            skLineSegment(sketch, "E20.direction2", {"start": v(15.14, 0) * mm, "end": v(15.14, 76.2) * mm, "construction": true});
            skSolve(sketch);
        }
        {
            var Q0;
            Q0=makeQuery(id+"F2.opExtrude","SWEPT_FACE",FACE,{"disambiguationData":[OSD([sQuery(id+"F1.wireOp",EDGE,"E4")])]});
            var sketch = newSketch(context, id + "F4", { "sketchPlane" : qUnion([Q0])});
            skPoint(sketch, "E21", {"position": v(-15.14, 19.05) * mm});
            skLineSegment(sketch, "E22", {"start": v(-15.14, 0) * mm, "end": v(-15.14, 1828.8) * mm, "construction": true});
            skCircle(sketch, "E23", {"center": v(-15.14, 19.05) * mm, "radius": 4.76 * mm});
            skCircle(sketch, "E24", {"center": v(-15.14, 0) * mm, "radius": 4.76 * mm});
            skPoint(sketch, "E25", {"position": v(-15.14, 38.1) * mm});
            skPoint(sketch, "E26", {"position": v(-15.14, 57.15) * mm});
            skArc(sketch, "E27", {"start": v(-10.38, 39.69) * mm, "mid": v(-15.14, 44.45) * mm, "end": v(-19.9, 39.69) * mm});
            skArc(sketch, "E28", {"start": v(-19.9, 36.51) * mm, "mid": v(-15.14, 31.75) * mm, "end": v(-10.38, 36.51) * mm});
            skLineSegment(sketch, "E29", {"start": v(-10.38, 39.69) * mm, "end": v(-10.38, 36.51) * mm});
            skLineSegment(sketch, "E30", {"start": v(-19.9, 39.69) * mm, "end": v(-19.9, 36.51) * mm});
            skArc(sketch, "E31", {"start": v(-10.38, 58.74) * mm, "mid": v(-15.14, 63.5) * mm, "end": v(-19.9, 58.74) * mm});
            skArc(sketch, "E32", {"start": v(-19.9, 55.56) * mm, "mid": v(-15.14, 50.8) * mm, "end": v(-10.38, 55.56) * mm});
            skLineSegment(sketch, "E33", {"start": v(-10.38, 58.74) * mm, "end": v(-10.38, 55.56) * mm});
            skLineSegment(sketch, "E34", {"start": v(-19.9, 58.74) * mm, "end": v(-19.9, 55.56) * mm});
            skPoint(sketch, "E35.0.1.0", {"position": v(-15.14, 133.35) * mm});
            skArc(sketch, "E35.0.1.1", {"start": v(-10.38, 134.94) * mm, "mid": v(-15.14, 139.7) * mm, "end": v(-19.9, 134.94) * mm});
            skPoint(sketch, "E35.0.1.2", {"position": v(-15.14, 114.3) * mm});
            skPoint(sketch, "E35.0.1.3", {"position": v(-15.14, 95.25) * mm});
            skArc(sketch, "E35.0.1.4", {"start": v(-19.9, 131.76) * mm, "mid": v(-15.14, 127) * mm, "end": v(-10.38, 131.76) * mm});
            skCircle(sketch, "E35.0.1.5", {"center": v(-15.14, 95.25) * mm, "radius": 4.76 * mm});
            skCircle(sketch, "E35.0.1.6", {"center": v(-15.14, 76.2) * mm, "radius": 4.76 * mm});
            skArc(sketch, "E35.0.1.7", {"start": v(-10.38, 115.89) * mm, "mid": v(-15.14, 120.65) * mm, "end": v(-19.9, 115.89) * mm});
            skArc(sketch, "E35.0.1.8", {"start": v(-19.9, 112.71) * mm, "mid": v(-15.14, 107.95) * mm, "end": v(-10.38, 112.71) * mm});
            skPoint(sketch, "E35.0.1.9", {"position": v(-15.14, 133.35) * mm});
            skPoint(sketch, "E35.0.1.10", {"position": v(-15.14, 114.3) * mm});
            skLineSegment(sketch, "E35.0.1.11", {"start": v(-19.9, 134.94) * mm, "end": v(-19.9, 131.76) * mm});
            skLineSegment(sketch, "E35.0.1.12", {"start": v(-10.38, 134.94) * mm, "end": v(-10.38, 131.76) * mm});
            skLineSegment(sketch, "E35.0.1.13", {"start": v(-10.38, 115.89) * mm, "end": v(-10.38, 112.71) * mm});
            skLineSegment(sketch, "E35.0.1.14", {"start": v(-19.9, 115.89) * mm, "end": v(-19.9, 112.71) * mm});
            skPoint(sketch, "E35.0.2.0", {"position": v(-15.14, 209.55) * mm});
            skArc(sketch, "E35.0.2.1", {"start": v(-10.38, 211.14) * mm, "mid": v(-15.14, 215.9) * mm, "end": v(-19.9, 211.14) * mm});
            skPoint(sketch, "E35.0.2.2", {"position": v(-15.14, 190.5) * mm});
            skPoint(sketch, "E35.0.2.3", {"position": v(-15.14, 171.45) * mm});
            skArc(sketch, "E35.0.2.4", {"start": v(-19.9, 207.96) * mm, "mid": v(-15.14, 203.2) * mm, "end": v(-10.38, 207.96) * mm});
            skCircle(sketch, "E35.0.2.5", {"center": v(-15.14, 171.45) * mm, "radius": 4.76 * mm});
            skCircle(sketch, "E35.0.2.6", {"center": v(-15.14, 152.4) * mm, "radius": 4.76 * mm});
            skArc(sketch, "E35.0.2.7", {"start": v(-10.38, 192.09) * mm, "mid": v(-15.14, 196.85) * mm, "end": v(-19.9, 192.09) * mm});
            skArc(sketch, "E35.0.2.8", {"start": v(-19.9, 188.91) * mm, "mid": v(-15.14, 184.15) * mm, "end": v(-10.38, 188.91) * mm});
            skPoint(sketch, "E35.0.2.9", {"position": v(-15.14, 209.55) * mm});
            skPoint(sketch, "E35.0.2.10", {"position": v(-15.14, 190.5) * mm});
            skLineSegment(sketch, "E35.0.2.11", {"start": v(-19.9, 211.14) * mm, "end": v(-19.9, 207.96) * mm});
            skLineSegment(sketch, "E35.0.2.12", {"start": v(-10.38, 211.14) * mm, "end": v(-10.38, 207.96) * mm});
            skLineSegment(sketch, "E35.0.2.13", {"start": v(-10.38, 192.09) * mm, "end": v(-10.38, 188.91) * mm});
            skLineSegment(sketch, "E35.0.2.14", {"start": v(-19.9, 192.09) * mm, "end": v(-19.9, 188.91) * mm});
            skPoint(sketch, "E35.0.3.0", {"position": v(-15.14, 285.75) * mm});
            skArc(sketch, "E35.0.3.1", {"start": v(-10.38, 287.34) * mm, "mid": v(-15.14, 292.1) * mm, "end": v(-19.9, 287.34) * mm});
            skPoint(sketch, "E35.0.3.2", {"position": v(-15.14, 266.7) * mm});
            skPoint(sketch, "E35.0.3.3", {"position": v(-15.14, 247.65) * mm});
            skArc(sketch, "E35.0.3.4", {"start": v(-19.9, 284.16) * mm, "mid": v(-15.14, 279.4) * mm, "end": v(-10.38, 284.16) * mm});
            skCircle(sketch, "E35.0.3.5", {"center": v(-15.14, 247.65) * mm, "radius": 4.76 * mm});
            skCircle(sketch, "E35.0.3.6", {"center": v(-15.14, 228.6) * mm, "radius": 4.76 * mm});
            skArc(sketch, "E35.0.3.7", {"start": v(-10.38, 268.29) * mm, "mid": v(-15.14, 273.05) * mm, "end": v(-19.9, 268.29) * mm});
            skArc(sketch, "E35.0.3.8", {"start": v(-19.9, 265.11) * mm, "mid": v(-15.14, 260.35) * mm, "end": v(-10.38, 265.11) * mm});
            skPoint(sketch, "E35.0.3.9", {"position": v(-15.14, 285.75) * mm});
            skPoint(sketch, "E35.0.3.10", {"position": v(-15.14, 266.7) * mm});
            skLineSegment(sketch, "E35.0.3.11", {"start": v(-19.9, 287.34) * mm, "end": v(-19.9, 284.16) * mm});
            skLineSegment(sketch, "E35.0.3.12", {"start": v(-10.38, 287.34) * mm, "end": v(-10.38, 284.16) * mm});
            skLineSegment(sketch, "E35.0.3.13", {"start": v(-10.38, 268.29) * mm, "end": v(-10.38, 265.11) * mm});
            skLineSegment(sketch, "E35.0.3.14", {"start": v(-19.9, 268.29) * mm, "end": v(-19.9, 265.11) * mm});
            skPoint(sketch, "E35.0.4.0", {"position": v(-15.14, 361.95) * mm});
            skArc(sketch, "E35.0.4.1", {"start": v(-10.38, 363.54) * mm, "mid": v(-15.14, 368.3) * mm, "end": v(-19.9, 363.54) * mm});
            skPoint(sketch, "E35.0.4.2", {"position": v(-15.14, 342.9) * mm});
            skPoint(sketch, "E35.0.4.3", {"position": v(-15.14, 323.85) * mm});
            skArc(sketch, "E35.0.4.4", {"start": v(-19.9, 360.36) * mm, "mid": v(-15.14, 355.6) * mm, "end": v(-10.38, 360.36) * mm});
            skCircle(sketch, "E35.0.4.5", {"center": v(-15.14, 323.85) * mm, "radius": 4.76 * mm});
            skCircle(sketch, "E35.0.4.6", {"center": v(-15.14, 304.8) * mm, "radius": 4.76 * mm});
            skArc(sketch, "E35.0.4.7", {"start": v(-10.38, 344.49) * mm, "mid": v(-15.14, 349.25) * mm, "end": v(-19.9, 344.49) * mm});
            skArc(sketch, "E35.0.4.8", {"start": v(-19.9, 341.31) * mm, "mid": v(-15.14, 336.55) * mm, "end": v(-10.38, 341.31) * mm});
            skPoint(sketch, "E35.0.4.9", {"position": v(-15.14, 361.95) * mm});
            skPoint(sketch, "E35.0.4.10", {"position": v(-15.14, 342.9) * mm});
            skLineSegment(sketch, "E35.0.4.11", {"start": v(-19.9, 363.54) * mm, "end": v(-19.9, 360.36) * mm});
            skLineSegment(sketch, "E35.0.4.12", {"start": v(-10.38, 363.54) * mm, "end": v(-10.38, 360.36) * mm});
            skLineSegment(sketch, "E35.0.4.13", {"start": v(-10.38, 344.49) * mm, "end": v(-10.38, 341.31) * mm});
            skLineSegment(sketch, "E35.0.4.14", {"start": v(-19.9, 344.49) * mm, "end": v(-19.9, 341.31) * mm});
            skPoint(sketch, "E35.0.5.0", {"position": v(-15.14, 438.15) * mm});
            skArc(sketch, "E35.0.5.1", {"start": v(-10.38, 439.74) * mm, "mid": v(-15.14, 444.5) * mm, "end": v(-19.9, 439.74) * mm});
            skPoint(sketch, "E35.0.5.2", {"position": v(-15.14, 419.1) * mm});
            skPoint(sketch, "E35.0.5.3", {"position": v(-15.14, 400.05) * mm});
            skArc(sketch, "E35.0.5.4", {"start": v(-19.9, 436.56) * mm, "mid": v(-15.14, 431.8) * mm, "end": v(-10.38, 436.56) * mm});
            skCircle(sketch, "E35.0.5.5", {"center": v(-15.14, 400.05) * mm, "radius": 4.76 * mm});
            skCircle(sketch, "E35.0.5.6", {"center": v(-15.14, 381) * mm, "radius": 4.76 * mm});
            skArc(sketch, "E35.0.5.7", {"start": v(-10.38, 420.69) * mm, "mid": v(-15.14, 425.45) * mm, "end": v(-19.9, 420.69) * mm});
            skArc(sketch, "E35.0.5.8", {"start": v(-19.9, 417.51) * mm, "mid": v(-15.14, 412.75) * mm, "end": v(-10.38, 417.51) * mm});
            skPoint(sketch, "E35.0.5.9", {"position": v(-15.14, 438.15) * mm});
            skPoint(sketch, "E35.0.5.10", {"position": v(-15.14, 419.1) * mm});
            skLineSegment(sketch, "E35.0.5.11", {"start": v(-19.9, 439.74) * mm, "end": v(-19.9, 436.56) * mm});
            skLineSegment(sketch, "E35.0.5.12", {"start": v(-10.38, 439.74) * mm, "end": v(-10.38, 436.56) * mm});
            skLineSegment(sketch, "E35.0.5.13", {"start": v(-10.38, 420.69) * mm, "end": v(-10.38, 417.51) * mm});
            skLineSegment(sketch, "E35.0.5.14", {"start": v(-19.9, 420.69) * mm, "end": v(-19.9, 417.51) * mm});
            skPoint(sketch, "E35.0.6.0", {"position": v(-15.14, 514.35) * mm});
            skArc(sketch, "E35.0.6.1", {"start": v(-10.38, 515.94) * mm, "mid": v(-15.14, 520.7) * mm, "end": v(-19.9, 515.94) * mm});
            skPoint(sketch, "E35.0.6.2", {"position": v(-15.14, 495.3) * mm});
            skPoint(sketch, "E35.0.6.3", {"position": v(-15.14, 476.25) * mm});
            skArc(sketch, "E35.0.6.4", {"start": v(-19.9, 512.76) * mm, "mid": v(-15.14, 508) * mm, "end": v(-10.38, 512.76) * mm});
            skCircle(sketch, "E35.0.6.5", {"center": v(-15.14, 476.25) * mm, "radius": 4.76 * mm});
            skCircle(sketch, "E35.0.6.6", {"center": v(-15.14, 457.2) * mm, "radius": 4.76 * mm});
            skArc(sketch, "E35.0.6.7", {"start": v(-10.38, 496.89) * mm, "mid": v(-15.14, 501.65) * mm, "end": v(-19.9, 496.89) * mm});
            skArc(sketch, "E35.0.6.8", {"start": v(-19.9, 493.71) * mm, "mid": v(-15.14, 488.95) * mm, "end": v(-10.38, 493.71) * mm});
            skPoint(sketch, "E35.0.6.9", {"position": v(-15.14, 514.35) * mm});
            skPoint(sketch, "E35.0.6.10", {"position": v(-15.14, 495.3) * mm});
            skLineSegment(sketch, "E35.0.6.11", {"start": v(-19.9, 515.94) * mm, "end": v(-19.9, 512.76) * mm});
            skLineSegment(sketch, "E35.0.6.12", {"start": v(-10.38, 515.94) * mm, "end": v(-10.38, 512.76) * mm});
            skLineSegment(sketch, "E35.0.6.13", {"start": v(-10.38, 496.89) * mm, "end": v(-10.38, 493.71) * mm});
            skLineSegment(sketch, "E35.0.6.14", {"start": v(-19.9, 496.89) * mm, "end": v(-19.9, 493.71) * mm});
            skPoint(sketch, "E35.0.7.0", {"position": v(-15.14, 590.55) * mm});
            skArc(sketch, "E35.0.7.1", {"start": v(-10.38, 592.14) * mm, "mid": v(-15.14, 596.9) * mm, "end": v(-19.9, 592.14) * mm});
            skPoint(sketch, "E35.0.7.2", {"position": v(-15.14, 571.5) * mm});
            skPoint(sketch, "E35.0.7.3", {"position": v(-15.14, 552.45) * mm});
            skArc(sketch, "E35.0.7.4", {"start": v(-19.9, 588.96) * mm, "mid": v(-15.14, 584.2) * mm, "end": v(-10.38, 588.96) * mm});
            skCircle(sketch, "E35.0.7.5", {"center": v(-15.14, 552.45) * mm, "radius": 4.76 * mm});
            skCircle(sketch, "E35.0.7.6", {"center": v(-15.14, 533.4) * mm, "radius": 4.76 * mm});
            skArc(sketch, "E35.0.7.7", {"start": v(-10.38, 573.09) * mm, "mid": v(-15.14, 577.85) * mm, "end": v(-19.9, 573.09) * mm});
            skArc(sketch, "E35.0.7.8", {"start": v(-19.9, 569.91) * mm, "mid": v(-15.14, 565.15) * mm, "end": v(-10.38, 569.91) * mm});
            skPoint(sketch, "E35.0.7.9", {"position": v(-15.14, 590.55) * mm});
            skPoint(sketch, "E35.0.7.10", {"position": v(-15.14, 571.5) * mm});
            skLineSegment(sketch, "E35.0.7.11", {"start": v(-19.9, 592.14) * mm, "end": v(-19.9, 588.96) * mm});
            skLineSegment(sketch, "E35.0.7.12", {"start": v(-10.38, 592.14) * mm, "end": v(-10.38, 588.96) * mm});
            skLineSegment(sketch, "E35.0.7.13", {"start": v(-10.38, 573.09) * mm, "end": v(-10.38, 569.91) * mm});
            skLineSegment(sketch, "E35.0.7.14", {"start": v(-19.9, 573.09) * mm, "end": v(-19.9, 569.91) * mm});
            skPoint(sketch, "E35.0.8.0", {"position": v(-15.14, 666.75) * mm});
            skArc(sketch, "E35.0.8.1", {"start": v(-10.38, 668.34) * mm, "mid": v(-15.14, 673.1) * mm, "end": v(-19.9, 668.34) * mm});
            skPoint(sketch, "E35.0.8.2", {"position": v(-15.14, 647.7) * mm});
            skPoint(sketch, "E35.0.8.3", {"position": v(-15.14, 628.65) * mm});
            skArc(sketch, "E35.0.8.4", {"start": v(-19.9, 665.16) * mm, "mid": v(-15.14, 660.4) * mm, "end": v(-10.38, 665.16) * mm});
            skCircle(sketch, "E35.0.8.5", {"center": v(-15.14, 628.65) * mm, "radius": 4.76 * mm});
            skCircle(sketch, "E35.0.8.6", {"center": v(-15.14, 609.6) * mm, "radius": 4.76 * mm});
            skArc(sketch, "E35.0.8.7", {"start": v(-10.38, 649.29) * mm, "mid": v(-15.14, 654.05) * mm, "end": v(-19.9, 649.29) * mm});
            skArc(sketch, "E35.0.8.8", {"start": v(-19.9, 646.11) * mm, "mid": v(-15.14, 641.35) * mm, "end": v(-10.38, 646.11) * mm});
            skPoint(sketch, "E35.0.8.9", {"position": v(-15.14, 666.75) * mm});
            skPoint(sketch, "E35.0.8.10", {"position": v(-15.14, 647.7) * mm});
            skLineSegment(sketch, "E35.0.8.11", {"start": v(-19.9, 668.34) * mm, "end": v(-19.9, 665.16) * mm});
            skLineSegment(sketch, "E35.0.8.12", {"start": v(-10.38, 668.34) * mm, "end": v(-10.38, 665.16) * mm});
            skLineSegment(sketch, "E35.0.8.13", {"start": v(-10.38, 649.29) * mm, "end": v(-10.38, 646.11) * mm});
            skLineSegment(sketch, "E35.0.8.14", {"start": v(-19.9, 649.29) * mm, "end": v(-19.9, 646.11) * mm});
            skPoint(sketch, "E35.0.9.0", {"position": v(-15.14, 742.95) * mm});
            skArc(sketch, "E35.0.9.1", {"start": v(-10.38, 744.54) * mm, "mid": v(-15.14, 749.3) * mm, "end": v(-19.9, 744.54) * mm});
            skPoint(sketch, "E35.0.9.2", {"position": v(-15.14, 723.9) * mm});
            skPoint(sketch, "E35.0.9.3", {"position": v(-15.14, 704.85) * mm});
            skArc(sketch, "E35.0.9.4", {"start": v(-19.9, 741.36) * mm, "mid": v(-15.14, 736.6) * mm, "end": v(-10.38, 741.36) * mm});
            skCircle(sketch, "E35.0.9.5", {"center": v(-15.14, 704.85) * mm, "radius": 4.76 * mm});
            skCircle(sketch, "E35.0.9.6", {"center": v(-15.14, 685.8) * mm, "radius": 4.76 * mm});
            skArc(sketch, "E35.0.9.7", {"start": v(-10.38, 725.49) * mm, "mid": v(-15.14, 730.25) * mm, "end": v(-19.9, 725.49) * mm});
            skArc(sketch, "E35.0.9.8", {"start": v(-19.9, 722.31) * mm, "mid": v(-15.14, 717.55) * mm, "end": v(-10.38, 722.31) * mm});
            skPoint(sketch, "E35.0.9.9", {"position": v(-15.14, 742.95) * mm});
            skPoint(sketch, "E35.0.9.10", {"position": v(-15.14, 723.9) * mm});
            skLineSegment(sketch, "E35.0.9.11", {"start": v(-19.9, 744.54) * mm, "end": v(-19.9, 741.36) * mm});
            skLineSegment(sketch, "E35.0.9.12", {"start": v(-10.38, 744.54) * mm, "end": v(-10.38, 741.36) * mm});
            skLineSegment(sketch, "E35.0.9.13", {"start": v(-10.38, 725.49) * mm, "end": v(-10.38, 722.31) * mm});
            skLineSegment(sketch, "E35.0.9.14", {"start": v(-19.9, 725.49) * mm, "end": v(-19.9, 722.31) * mm});
            skPoint(sketch, "E35.0.10.0", {"position": v(-15.14, 819.15) * mm});
            skArc(sketch, "E35.0.10.1", {"start": v(-10.38, 820.74) * mm, "mid": v(-15.14, 825.5) * mm, "end": v(-19.9, 820.74) * mm});
            skPoint(sketch, "E35.0.10.2", {"position": v(-15.14, 800.1) * mm});
            skPoint(sketch, "E35.0.10.3", {"position": v(-15.14, 781.05) * mm});
            skArc(sketch, "E35.0.10.4", {"start": v(-19.9, 817.56) * mm, "mid": v(-15.14, 812.8) * mm, "end": v(-10.38, 817.56) * mm});
            skCircle(sketch, "E35.0.10.5", {"center": v(-15.14, 781.05) * mm, "radius": 4.76 * mm});
            skCircle(sketch, "E35.0.10.6", {"center": v(-15.14, 762) * mm, "radius": 4.76 * mm});
            skArc(sketch, "E35.0.10.7", {"start": v(-10.38, 801.69) * mm, "mid": v(-15.14, 806.45) * mm, "end": v(-19.9, 801.69) * mm});
            skArc(sketch, "E35.0.10.8", {"start": v(-19.9, 798.51) * mm, "mid": v(-15.14, 793.75) * mm, "end": v(-10.38, 798.51) * mm});
            skPoint(sketch, "E35.0.10.9", {"position": v(-15.14, 819.15) * mm});
            skPoint(sketch, "E35.0.10.10", {"position": v(-15.14, 800.1) * mm});
            skLineSegment(sketch, "E35.0.10.11", {"start": v(-19.9, 820.74) * mm, "end": v(-19.9, 817.56) * mm});
            skLineSegment(sketch, "E35.0.10.12", {"start": v(-10.38, 820.74) * mm, "end": v(-10.38, 817.56) * mm});
            skLineSegment(sketch, "E35.0.10.13", {"start": v(-10.38, 801.69) * mm, "end": v(-10.38, 798.51) * mm});
            skLineSegment(sketch, "E35.0.10.14", {"start": v(-19.9, 801.69) * mm, "end": v(-19.9, 798.51) * mm});
            skPoint(sketch, "E35.0.11.0", {"position": v(-15.14, 895.35) * mm});
            skArc(sketch, "E35.0.11.1", {"start": v(-10.38, 896.94) * mm, "mid": v(-15.14, 901.7) * mm, "end": v(-19.9, 896.94) * mm});
            skPoint(sketch, "E35.0.11.2", {"position": v(-15.14, 876.3) * mm});
            skPoint(sketch, "E35.0.11.3", {"position": v(-15.14, 857.25) * mm});
            skArc(sketch, "E35.0.11.4", {"start": v(-19.9, 893.76) * mm, "mid": v(-15.14, 889) * mm, "end": v(-10.38, 893.76) * mm});
            skCircle(sketch, "E35.0.11.5", {"center": v(-15.14, 857.25) * mm, "radius": 4.76 * mm});
            skCircle(sketch, "E35.0.11.6", {"center": v(-15.14, 838.2) * mm, "radius": 4.76 * mm});
            skArc(sketch, "E35.0.11.7", {"start": v(-10.38, 877.89) * mm, "mid": v(-15.14, 882.65) * mm, "end": v(-19.9, 877.89) * mm});
            skArc(sketch, "E35.0.11.8", {"start": v(-19.9, 874.71) * mm, "mid": v(-15.14, 869.95) * mm, "end": v(-10.38, 874.71) * mm});
            skPoint(sketch, "E35.0.11.9", {"position": v(-15.14, 895.35) * mm});
            skPoint(sketch, "E35.0.11.10", {"position": v(-15.14, 876.3) * mm});
            skLineSegment(sketch, "E35.0.11.11", {"start": v(-19.9, 896.94) * mm, "end": v(-19.9, 893.76) * mm});
            skLineSegment(sketch, "E35.0.11.12", {"start": v(-10.38, 896.94) * mm, "end": v(-10.38, 893.76) * mm});
            skLineSegment(sketch, "E35.0.11.13", {"start": v(-10.38, 877.89) * mm, "end": v(-10.38, 874.71) * mm});
            skLineSegment(sketch, "E35.0.11.14", {"start": v(-19.9, 877.89) * mm, "end": v(-19.9, 874.71) * mm});
            skPoint(sketch, "E35.0.12.0", {"position": v(-15.14, 971.55) * mm});
            skArc(sketch, "E35.0.12.1", {"start": v(-10.38, 973.14) * mm, "mid": v(-15.14, 977.9) * mm, "end": v(-19.9, 973.14) * mm});
            skPoint(sketch, "E35.0.12.2", {"position": v(-15.14, 952.5) * mm});
            skPoint(sketch, "E35.0.12.3", {"position": v(-15.14, 933.45) * mm});
            skArc(sketch, "E35.0.12.4", {"start": v(-19.9, 969.96) * mm, "mid": v(-15.14, 965.2) * mm, "end": v(-10.38, 969.96) * mm});
            skCircle(sketch, "E35.0.12.5", {"center": v(-15.14, 933.45) * mm, "radius": 4.76 * mm});
            skCircle(sketch, "E35.0.12.6", {"center": v(-15.14, 914.4) * mm, "radius": 4.76 * mm});
            skArc(sketch, "E35.0.12.7", {"start": v(-10.38, 954.09) * mm, "mid": v(-15.14, 958.85) * mm, "end": v(-19.9, 954.09) * mm});
            skArc(sketch, "E35.0.12.8", {"start": v(-19.9, 950.91) * mm, "mid": v(-15.14, 946.15) * mm, "end": v(-10.38, 950.91) * mm});
            skPoint(sketch, "E35.0.12.9", {"position": v(-15.14, 971.55) * mm});
            skPoint(sketch, "E35.0.12.10", {"position": v(-15.14, 952.5) * mm});
            skLineSegment(sketch, "E35.0.12.11", {"start": v(-19.9, 973.14) * mm, "end": v(-19.9, 969.96) * mm});
            skLineSegment(sketch, "E35.0.12.12", {"start": v(-10.38, 973.14) * mm, "end": v(-10.38, 969.96) * mm});
            skLineSegment(sketch, "E35.0.12.13", {"start": v(-10.38, 954.09) * mm, "end": v(-10.38, 950.91) * mm});
            skLineSegment(sketch, "E35.0.12.14", {"start": v(-19.9, 954.09) * mm, "end": v(-19.9, 950.91) * mm});
            skPoint(sketch, "E35.0.13.0", {"position": v(-15.14, 1047.75) * mm});
            skArc(sketch, "E35.0.13.1", {"start": v(-10.38, 1049.34) * mm, "mid": v(-15.14, 1054.1) * mm, "end": v(-19.9, 1049.34) * mm});
            skPoint(sketch, "E35.0.13.2", {"position": v(-15.14, 1028.7) * mm});
            skPoint(sketch, "E35.0.13.3", {"position": v(-15.14, 1009.65) * mm});
            skArc(sketch, "E35.0.13.4", {"start": v(-19.9, 1046.16) * mm, "mid": v(-15.14, 1041.4) * mm, "end": v(-10.38, 1046.16) * mm});
            skCircle(sketch, "E35.0.13.5", {"center": v(-15.14, 1009.65) * mm, "radius": 4.76 * mm});
            skCircle(sketch, "E35.0.13.6", {"center": v(-15.14, 990.6) * mm, "radius": 4.76 * mm});
            skArc(sketch, "E35.0.13.7", {"start": v(-10.38, 1030.29) * mm, "mid": v(-15.14, 1035.05) * mm, "end": v(-19.9, 1030.29) * mm});
            skArc(sketch, "E35.0.13.8", {"start": v(-19.9, 1027.11) * mm, "mid": v(-15.14, 1022.35) * mm, "end": v(-10.38, 1027.11) * mm});
            skPoint(sketch, "E35.0.13.9", {"position": v(-15.14, 1047.75) * mm});
            skPoint(sketch, "E35.0.13.10", {"position": v(-15.14, 1028.7) * mm});
            skLineSegment(sketch, "E35.0.13.11", {"start": v(-19.9, 1049.34) * mm, "end": v(-19.9, 1046.16) * mm});
            skLineSegment(sketch, "E35.0.13.12", {"start": v(-10.38, 1049.34) * mm, "end": v(-10.38, 1046.16) * mm});
            skLineSegment(sketch, "E35.0.13.13", {"start": v(-10.38, 1030.29) * mm, "end": v(-10.38, 1027.11) * mm});
            skLineSegment(sketch, "E35.0.13.14", {"start": v(-19.9, 1030.29) * mm, "end": v(-19.9, 1027.11) * mm});
            skPoint(sketch, "E35.0.14.0", {"position": v(-15.14, 1123.95) * mm});
            skArc(sketch, "E35.0.14.1", {"start": v(-10.38, 1125.54) * mm, "mid": v(-15.14, 1130.3) * mm, "end": v(-19.9, 1125.54) * mm});
            skPoint(sketch, "E35.0.14.2", {"position": v(-15.14, 1104.9) * mm});
            skPoint(sketch, "E35.0.14.3", {"position": v(-15.14, 1085.85) * mm});
            skArc(sketch, "E35.0.14.4", {"start": v(-19.9, 1122.36) * mm, "mid": v(-15.14, 1117.6) * mm, "end": v(-10.38, 1122.36) * mm});
            skCircle(sketch, "E35.0.14.5", {"center": v(-15.14, 1085.85) * mm, "radius": 4.76 * mm});
            skCircle(sketch, "E35.0.14.6", {"center": v(-15.14, 1066.8) * mm, "radius": 4.76 * mm});
            skArc(sketch, "E35.0.14.7", {"start": v(-10.38, 1106.49) * mm, "mid": v(-15.14, 1111.25) * mm, "end": v(-19.9, 1106.49) * mm});
            skArc(sketch, "E35.0.14.8", {"start": v(-19.9, 1103.31) * mm, "mid": v(-15.14, 1098.55) * mm, "end": v(-10.38, 1103.31) * mm});
            skPoint(sketch, "E35.0.14.9", {"position": v(-15.14, 1123.95) * mm});
            skPoint(sketch, "E35.0.14.10", {"position": v(-15.14, 1104.9) * mm});
            skLineSegment(sketch, "E35.0.14.11", {"start": v(-19.9, 1125.54) * mm, "end": v(-19.9, 1122.36) * mm});
            skLineSegment(sketch, "E35.0.14.12", {"start": v(-10.38, 1125.54) * mm, "end": v(-10.38, 1122.36) * mm});
            skLineSegment(sketch, "E35.0.14.13", {"start": v(-10.38, 1106.49) * mm, "end": v(-10.38, 1103.31) * mm});
            skLineSegment(sketch, "E35.0.14.14", {"start": v(-19.9, 1106.49) * mm, "end": v(-19.9, 1103.31) * mm});
            skPoint(sketch, "E35.0.15.0", {"position": v(-15.14, 1200.15) * mm});
            skArc(sketch, "E35.0.15.1", {"start": v(-10.38, 1201.74) * mm, "mid": v(-15.14, 1206.5) * mm, "end": v(-19.9, 1201.74) * mm});
            skPoint(sketch, "E35.0.15.2", {"position": v(-15.14, 1181.1) * mm});
            skPoint(sketch, "E35.0.15.3", {"position": v(-15.14, 1162.05) * mm});
            skArc(sketch, "E35.0.15.4", {"start": v(-19.9, 1198.56) * mm, "mid": v(-15.14, 1193.8) * mm, "end": v(-10.38, 1198.56) * mm});
            skCircle(sketch, "E35.0.15.5", {"center": v(-15.14, 1162.05) * mm, "radius": 4.76 * mm});
            skCircle(sketch, "E35.0.15.6", {"center": v(-15.14, 1143) * mm, "radius": 4.76 * mm});
            skArc(sketch, "E35.0.15.7", {"start": v(-10.38, 1182.69) * mm, "mid": v(-15.14, 1187.45) * mm, "end": v(-19.9, 1182.69) * mm});
            skArc(sketch, "E35.0.15.8", {"start": v(-19.9, 1179.51) * mm, "mid": v(-15.14, 1174.75) * mm, "end": v(-10.38, 1179.51) * mm});
            skPoint(sketch, "E35.0.15.9", {"position": v(-15.14, 1200.15) * mm});
            skPoint(sketch, "E35.0.15.10", {"position": v(-15.14, 1181.1) * mm});
            skLineSegment(sketch, "E35.0.15.11", {"start": v(-19.9, 1201.74) * mm, "end": v(-19.9, 1198.56) * mm});
            skLineSegment(sketch, "E35.0.15.12", {"start": v(-10.38, 1201.74) * mm, "end": v(-10.38, 1198.56) * mm});
            skLineSegment(sketch, "E35.0.15.13", {"start": v(-10.38, 1182.69) * mm, "end": v(-10.38, 1179.51) * mm});
            skLineSegment(sketch, "E35.0.15.14", {"start": v(-19.9, 1182.69) * mm, "end": v(-19.9, 1179.51) * mm});
            skPoint(sketch, "E35.0.16.0", {"position": v(-15.14, 1276.35) * mm});
            skArc(sketch, "E35.0.16.1", {"start": v(-10.38, 1277.94) * mm, "mid": v(-15.14, 1282.7) * mm, "end": v(-19.9, 1277.94) * mm});
            skPoint(sketch, "E35.0.16.2", {"position": v(-15.14, 1257.3) * mm});
            skPoint(sketch, "E35.0.16.3", {"position": v(-15.14, 1238.25) * mm});
            skArc(sketch, "E35.0.16.4", {"start": v(-19.9, 1274.76) * mm, "mid": v(-15.14, 1270) * mm, "end": v(-10.38, 1274.76) * mm});
            skCircle(sketch, "E35.0.16.5", {"center": v(-15.14, 1238.25) * mm, "radius": 4.76 * mm});
            skCircle(sketch, "E35.0.16.6", {"center": v(-15.14, 1219.2) * mm, "radius": 4.76 * mm});
            skArc(sketch, "E35.0.16.7", {"start": v(-10.38, 1258.89) * mm, "mid": v(-15.14, 1263.65) * mm, "end": v(-19.9, 1258.89) * mm});
            skArc(sketch, "E35.0.16.8", {"start": v(-19.9, 1255.71) * mm, "mid": v(-15.14, 1250.95) * mm, "end": v(-10.38, 1255.71) * mm});
            skPoint(sketch, "E35.0.16.9", {"position": v(-15.14, 1276.35) * mm});
            skPoint(sketch, "E35.0.16.10", {"position": v(-15.14, 1257.3) * mm});
            skLineSegment(sketch, "E35.0.16.11", {"start": v(-19.9, 1277.94) * mm, "end": v(-19.9, 1274.76) * mm});
            skLineSegment(sketch, "E35.0.16.12", {"start": v(-10.38, 1277.94) * mm, "end": v(-10.38, 1274.76) * mm});
            skLineSegment(sketch, "E35.0.16.13", {"start": v(-10.38, 1258.89) * mm, "end": v(-10.38, 1255.71) * mm});
            skLineSegment(sketch, "E35.0.16.14", {"start": v(-19.9, 1258.89) * mm, "end": v(-19.9, 1255.71) * mm});
            skPoint(sketch, "E35.0.17.0", {"position": v(-15.14, 1352.55) * mm});
            skArc(sketch, "E35.0.17.1", {"start": v(-10.38, 1354.14) * mm, "mid": v(-15.14, 1358.9) * mm, "end": v(-19.9, 1354.14) * mm});
            skPoint(sketch, "E35.0.17.2", {"position": v(-15.14, 1333.5) * mm});
            skPoint(sketch, "E35.0.17.3", {"position": v(-15.14, 1314.45) * mm});
            skArc(sketch, "E35.0.17.4", {"start": v(-19.9, 1350.96) * mm, "mid": v(-15.14, 1346.2) * mm, "end": v(-10.38, 1350.96) * mm});
            skCircle(sketch, "E35.0.17.5", {"center": v(-15.14, 1314.45) * mm, "radius": 4.76 * mm});
            skCircle(sketch, "E35.0.17.6", {"center": v(-15.14, 1295.4) * mm, "radius": 4.76 * mm});
            skArc(sketch, "E35.0.17.7", {"start": v(-10.38, 1335.09) * mm, "mid": v(-15.14, 1339.85) * mm, "end": v(-19.9, 1335.09) * mm});
            skArc(sketch, "E35.0.17.8", {"start": v(-19.9, 1331.91) * mm, "mid": v(-15.14, 1327.15) * mm, "end": v(-10.38, 1331.91) * mm});
            skPoint(sketch, "E35.0.17.9", {"position": v(-15.14, 1352.55) * mm});
            skPoint(sketch, "E35.0.17.10", {"position": v(-15.14, 1333.5) * mm});
            skLineSegment(sketch, "E35.0.17.11", {"start": v(-19.9, 1354.14) * mm, "end": v(-19.9, 1350.96) * mm});
            skLineSegment(sketch, "E35.0.17.12", {"start": v(-10.38, 1354.14) * mm, "end": v(-10.38, 1350.96) * mm});
            skLineSegment(sketch, "E35.0.17.13", {"start": v(-10.38, 1335.09) * mm, "end": v(-10.38, 1331.91) * mm});
            skLineSegment(sketch, "E35.0.17.14", {"start": v(-19.9, 1335.09) * mm, "end": v(-19.9, 1331.91) * mm});
            skPoint(sketch, "E35.0.18.0", {"position": v(-15.14, 1428.75) * mm});
            skArc(sketch, "E35.0.18.1", {"start": v(-10.38, 1430.34) * mm, "mid": v(-15.14, 1435.1) * mm, "end": v(-19.9, 1430.34) * mm});
            skPoint(sketch, "E35.0.18.2", {"position": v(-15.14, 1409.7) * mm});
            skPoint(sketch, "E35.0.18.3", {"position": v(-15.14, 1390.65) * mm});
            skArc(sketch, "E35.0.18.4", {"start": v(-19.9, 1427.16) * mm, "mid": v(-15.14, 1422.4) * mm, "end": v(-10.38, 1427.16) * mm});
            skCircle(sketch, "E35.0.18.5", {"center": v(-15.14, 1390.65) * mm, "radius": 4.76 * mm});
            skCircle(sketch, "E35.0.18.6", {"center": v(-15.14, 1371.6) * mm, "radius": 4.76 * mm});
            skArc(sketch, "E35.0.18.7", {"start": v(-10.38, 1411.29) * mm, "mid": v(-15.14, 1416.05) * mm, "end": v(-19.9, 1411.29) * mm});
            skArc(sketch, "E35.0.18.8", {"start": v(-19.9, 1408.11) * mm, "mid": v(-15.14, 1403.35) * mm, "end": v(-10.38, 1408.11) * mm});
            skPoint(sketch, "E35.0.18.9", {"position": v(-15.14, 1428.75) * mm});
            skPoint(sketch, "E35.0.18.10", {"position": v(-15.14, 1409.7) * mm});
            skLineSegment(sketch, "E35.0.18.11", {"start": v(-19.9, 1430.34) * mm, "end": v(-19.9, 1427.16) * mm});
            skLineSegment(sketch, "E35.0.18.12", {"start": v(-10.38, 1430.34) * mm, "end": v(-10.38, 1427.16) * mm});
            skLineSegment(sketch, "E35.0.18.13", {"start": v(-10.38, 1411.29) * mm, "end": v(-10.38, 1408.11) * mm});
            skLineSegment(sketch, "E35.0.18.14", {"start": v(-19.9, 1411.29) * mm, "end": v(-19.9, 1408.11) * mm});
            skPoint(sketch, "E35.0.19.0", {"position": v(-15.14, 1504.95) * mm});
            skArc(sketch, "E35.0.19.1", {"start": v(-10.38, 1506.54) * mm, "mid": v(-15.14, 1511.3) * mm, "end": v(-19.9, 1506.54) * mm});
            skPoint(sketch, "E35.0.19.2", {"position": v(-15.14, 1485.9) * mm});
            skPoint(sketch, "E35.0.19.3", {"position": v(-15.14, 1466.85) * mm});
            skArc(sketch, "E35.0.19.4", {"start": v(-19.9, 1503.36) * mm, "mid": v(-15.14, 1498.6) * mm, "end": v(-10.38, 1503.36) * mm});
            skCircle(sketch, "E35.0.19.5", {"center": v(-15.14, 1466.85) * mm, "radius": 4.76 * mm});
            skCircle(sketch, "E35.0.19.6", {"center": v(-15.14, 1447.8) * mm, "radius": 4.76 * mm});
            skArc(sketch, "E35.0.19.7", {"start": v(-10.38, 1487.49) * mm, "mid": v(-15.14, 1492.25) * mm, "end": v(-19.9, 1487.49) * mm});
            skArc(sketch, "E35.0.19.8", {"start": v(-19.9, 1484.31) * mm, "mid": v(-15.14, 1479.55) * mm, "end": v(-10.38, 1484.31) * mm});
            skPoint(sketch, "E35.0.19.9", {"position": v(-15.14, 1504.95) * mm});
            skPoint(sketch, "E35.0.19.10", {"position": v(-15.14, 1485.9) * mm});
            skLineSegment(sketch, "E35.0.19.11", {"start": v(-19.9, 1506.54) * mm, "end": v(-19.9, 1503.36) * mm});
            skLineSegment(sketch, "E35.0.19.12", {"start": v(-10.38, 1506.54) * mm, "end": v(-10.38, 1503.36) * mm});
            skLineSegment(sketch, "E35.0.19.13", {"start": v(-10.38, 1487.49) * mm, "end": v(-10.38, 1484.31) * mm});
            skLineSegment(sketch, "E35.0.19.14", {"start": v(-19.9, 1487.49) * mm, "end": v(-19.9, 1484.31) * mm});
            skPoint(sketch, "E35.0.20.0", {"position": v(-15.14, 1581.15) * mm});
            skArc(sketch, "E35.0.20.1", {"start": v(-10.38, 1582.74) * mm, "mid": v(-15.14, 1587.5) * mm, "end": v(-19.9, 1582.74) * mm});
            skPoint(sketch, "E35.0.20.2", {"position": v(-15.14, 1562.1) * mm});
            skPoint(sketch, "E35.0.20.3", {"position": v(-15.14, 1543.05) * mm});
            skArc(sketch, "E35.0.20.4", {"start": v(-19.9, 1579.56) * mm, "mid": v(-15.14, 1574.8) * mm, "end": v(-10.38, 1579.56) * mm});
            skCircle(sketch, "E35.0.20.5", {"center": v(-15.14, 1543.05) * mm, "radius": 4.76 * mm});
            skCircle(sketch, "E35.0.20.6", {"center": v(-15.14, 1524) * mm, "radius": 4.76 * mm});
            skArc(sketch, "E35.0.20.7", {"start": v(-10.38, 1563.69) * mm, "mid": v(-15.14, 1568.45) * mm, "end": v(-19.9, 1563.69) * mm});
            skArc(sketch, "E35.0.20.8", {"start": v(-19.9, 1560.51) * mm, "mid": v(-15.14, 1555.75) * mm, "end": v(-10.38, 1560.51) * mm});
            skPoint(sketch, "E35.0.20.9", {"position": v(-15.14, 1581.15) * mm});
            skPoint(sketch, "E35.0.20.10", {"position": v(-15.14, 1562.1) * mm});
            skLineSegment(sketch, "E35.0.20.11", {"start": v(-19.9, 1582.74) * mm, "end": v(-19.9, 1579.56) * mm});
            skLineSegment(sketch, "E35.0.20.12", {"start": v(-10.38, 1582.74) * mm, "end": v(-10.38, 1579.56) * mm});
            skLineSegment(sketch, "E35.0.20.13", {"start": v(-10.38, 1563.69) * mm, "end": v(-10.38, 1560.51) * mm});
            skLineSegment(sketch, "E35.0.20.14", {"start": v(-19.9, 1563.69) * mm, "end": v(-19.9, 1560.51) * mm});
            skPoint(sketch, "E35.0.21.0", {"position": v(-15.14, 1657.35) * mm});
            skArc(sketch, "E35.0.21.1", {"start": v(-10.38, 1658.94) * mm, "mid": v(-15.14, 1663.7) * mm, "end": v(-19.9, 1658.94) * mm});
            skPoint(sketch, "E35.0.21.2", {"position": v(-15.14, 1638.3) * mm});
            skPoint(sketch, "E35.0.21.3", {"position": v(-15.14, 1619.25) * mm});
            skArc(sketch, "E35.0.21.4", {"start": v(-19.9, 1655.76) * mm, "mid": v(-15.14, 1651) * mm, "end": v(-10.38, 1655.76) * mm});
            skCircle(sketch, "E35.0.21.5", {"center": v(-15.14, 1619.25) * mm, "radius": 4.76 * mm});
            skCircle(sketch, "E35.0.21.6", {"center": v(-15.14, 1600.2) * mm, "radius": 4.76 * mm});
            skArc(sketch, "E35.0.21.7", {"start": v(-10.38, 1639.89) * mm, "mid": v(-15.14, 1644.65) * mm, "end": v(-19.9, 1639.89) * mm});
            skArc(sketch, "E35.0.21.8", {"start": v(-19.9, 1636.71) * mm, "mid": v(-15.14, 1631.95) * mm, "end": v(-10.38, 1636.71) * mm});
            skPoint(sketch, "E35.0.21.9", {"position": v(-15.14, 1657.35) * mm});
            skPoint(sketch, "E35.0.21.10", {"position": v(-15.14, 1638.3) * mm});
            skLineSegment(sketch, "E35.0.21.11", {"start": v(-19.9, 1658.94) * mm, "end": v(-19.9, 1655.76) * mm});
            skLineSegment(sketch, "E35.0.21.12", {"start": v(-10.38, 1658.94) * mm, "end": v(-10.38, 1655.76) * mm});
            skLineSegment(sketch, "E35.0.21.13", {"start": v(-10.38, 1639.89) * mm, "end": v(-10.38, 1636.71) * mm});
            skLineSegment(sketch, "E35.0.21.14", {"start": v(-19.9, 1639.89) * mm, "end": v(-19.9, 1636.71) * mm});
            skPoint(sketch, "E35.0.22.0", {"position": v(-15.14, 1733.55) * mm});
            skArc(sketch, "E35.0.22.1", {"start": v(-10.38, 1735.14) * mm, "mid": v(-15.14, 1739.9) * mm, "end": v(-19.9, 1735.14) * mm});
            skPoint(sketch, "E35.0.22.2", {"position": v(-15.14, 1714.5) * mm});
            skPoint(sketch, "E35.0.22.3", {"position": v(-15.14, 1695.45) * mm});
            skArc(sketch, "E35.0.22.4", {"start": v(-19.9, 1731.96) * mm, "mid": v(-15.14, 1727.2) * mm, "end": v(-10.38, 1731.96) * mm});
            skCircle(sketch, "E35.0.22.5", {"center": v(-15.14, 1695.45) * mm, "radius": 4.76 * mm});
            skCircle(sketch, "E35.0.22.6", {"center": v(-15.14, 1676.4) * mm, "radius": 4.76 * mm});
            skArc(sketch, "E35.0.22.7", {"start": v(-10.38, 1716.09) * mm, "mid": v(-15.14, 1720.85) * mm, "end": v(-19.9, 1716.09) * mm});
            skArc(sketch, "E35.0.22.8", {"start": v(-19.9, 1712.91) * mm, "mid": v(-15.14, 1708.15) * mm, "end": v(-10.38, 1712.91) * mm});
            skPoint(sketch, "E35.0.22.9", {"position": v(-15.14, 1733.55) * mm});
            skPoint(sketch, "E35.0.22.10", {"position": v(-15.14, 1714.5) * mm});
            skLineSegment(sketch, "E35.0.22.11", {"start": v(-19.9, 1735.14) * mm, "end": v(-19.9, 1731.96) * mm});
            skLineSegment(sketch, "E35.0.22.12", {"start": v(-10.38, 1735.14) * mm, "end": v(-10.38, 1731.96) * mm});
            skLineSegment(sketch, "E35.0.22.13", {"start": v(-10.38, 1716.09) * mm, "end": v(-10.38, 1712.91) * mm});
            skLineSegment(sketch, "E35.0.22.14", {"start": v(-19.9, 1716.09) * mm, "end": v(-19.9, 1712.91) * mm});
            skPoint(sketch, "E35.0.23.0", {"position": v(-15.14, 1809.75) * mm});
            skArc(sketch, "E35.0.23.1", {"start": v(-10.38, 1811.34) * mm, "mid": v(-15.14, 1816.1) * mm, "end": v(-19.9, 1811.34) * mm});
            skPoint(sketch, "E35.0.23.2", {"position": v(-15.14, 1790.7) * mm});
            skPoint(sketch, "E35.0.23.3", {"position": v(-15.14, 1771.65) * mm});
            skArc(sketch, "E35.0.23.4", {"start": v(-19.9, 1808.16) * mm, "mid": v(-15.14, 1803.4) * mm, "end": v(-10.38, 1808.16) * mm});
            skCircle(sketch, "E35.0.23.5", {"center": v(-15.14, 1771.65) * mm, "radius": 4.76 * mm});
            skCircle(sketch, "E35.0.23.6", {"center": v(-15.14, 1752.6) * mm, "radius": 4.76 * mm});
            skArc(sketch, "E35.0.23.7", {"start": v(-10.38, 1792.29) * mm, "mid": v(-15.14, 1797.05) * mm, "end": v(-19.9, 1792.29) * mm});
            skArc(sketch, "E35.0.23.8", {"start": v(-19.9, 1789.11) * mm, "mid": v(-15.14, 1784.35) * mm, "end": v(-10.38, 1789.11) * mm});
            skPoint(sketch, "E35.0.23.9", {"position": v(-15.14, 1809.75) * mm});
            skPoint(sketch, "E35.0.23.10", {"position": v(-15.14, 1790.7) * mm});
            skLineSegment(sketch, "E35.0.23.11", {"start": v(-19.9, 1811.34) * mm, "end": v(-19.9, 1808.16) * mm});
            skLineSegment(sketch, "E35.0.23.12", {"start": v(-10.38, 1811.34) * mm, "end": v(-10.38, 1808.16) * mm});
            skLineSegment(sketch, "E35.0.23.13", {"start": v(-10.38, 1792.29) * mm, "end": v(-10.38, 1789.11) * mm});
            skLineSegment(sketch, "E35.0.23.14", {"start": v(-19.9, 1792.29) * mm, "end": v(-19.9, 1789.11) * mm});
            skLineSegment(sketch, "E35.direction1", {"start": v(-15.14, 0) * mm, "end": v(10.99, 0) * mm, "construction": true});
            skLineSegment(sketch, "E35.direction2", {"start": v(-15.14, 0) * mm, "end": v(-15.14, 76.2) * mm, "construction": true});
            skSolve(sketch);
        }
        {
            var Q0;
            Q0 = qSketchRegion(id + "F3", true);
            extrude(context, id + "F5", {"entities" : qUnion([Q0]), "operationType" : NewBodyOperationType.REMOVE, "endBound" : BoundingType.THROUGH_ALL, "oppositeDirection" : true, "depth" : 25.4 * mm, "offsetDistance" : 25.4 * mm});
        }
        {
            var Q0;
            Q0 = qSketchRegion(id + "F4", true);
            extrude(context, id + "F6", {"entities" : qUnion([Q0]), "operationType" : NewBodyOperationType.REMOVE, "endBound" : BoundingType.THROUGH_ALL, "oppositeDirection" : true, "depth" : 25.4 * mm, "offsetDistance" : 25.4 * mm});
        }
    });
